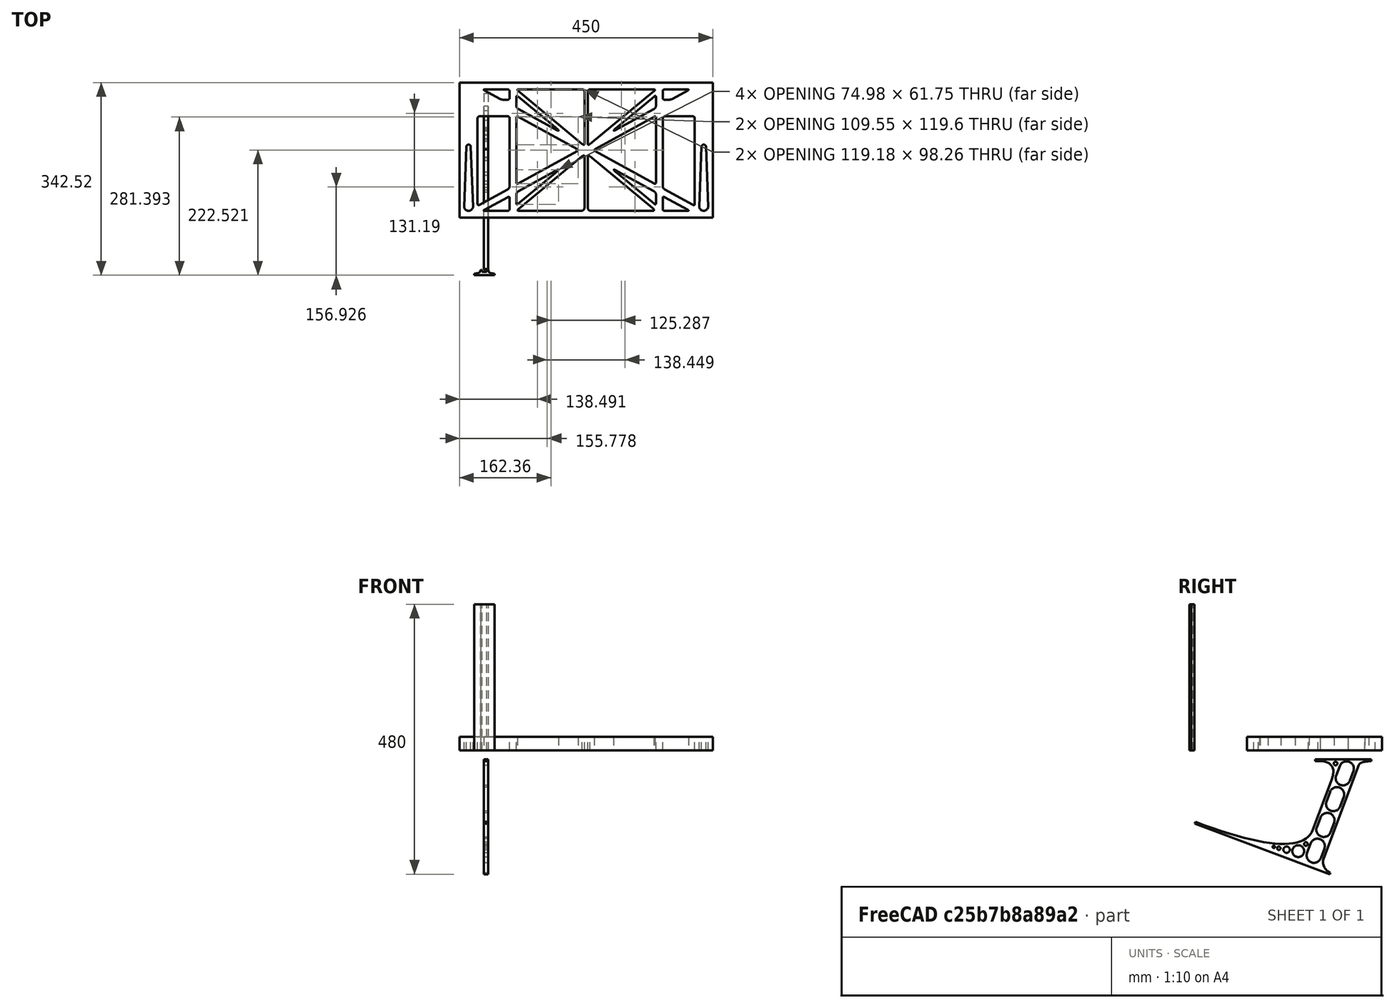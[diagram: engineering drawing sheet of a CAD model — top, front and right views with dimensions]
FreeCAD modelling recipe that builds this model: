
FCSTD DOCUMENT  (FreeCAD 0.19R0.19.2)
Label: laptopStand161FCStd
License: All rights reserved
LicenseURL: http://en.wikipedia.org/wiki/All_rights_reserved
objects: Sketcher::SketchObject×4, Part::Extrusion×3
note: 7 computed .brp shape members not serialized (recipe doc carries the construction recipe); baked Part::Feature solids carry a one-line shape summary decoded from their .brp

FEATURE [Sketcher::SketchObject] Sketch
  FullyConstrained = false
  sketch-geometry (349):
    g0: LineSegment StartX=-10.9272 StartY=-82.7794 StartZ=0 EndX=46.0728 EndY=-51.4823 EndZ=0
    g1: LineSegment StartX=-10.9272 StartY=76.4095 StartZ=0 EndX=-10.9272 EndY=-82.7794 EndZ=0
    g2: LineSegment StartX=46.0728 StartY=76.4095 StartZ=0 EndX=46.0728 EndY=-51.4823 EndZ=0
    g3: LineSegment StartX=-42.9272 StartY=136.221 StartZ=0 EndX=-42.9272 EndY=-103.779 EndZ=0
    g4: LineSegment StartX=407.073 StartY=136.221 StartZ=0 EndX=407.073 EndY=-103.779 EndZ=0
    g5: ArcOfCircle CenterX=-26.9272 CenterY=-83.7794 CenterZ=0 NormalX=0 NormalY=0 NormalZ=1 AngleXU=0 Radius=8 StartAngle=3.14159 EndAngle=6.28319
    g6: ArcOfCircle CenterX=391.073 CenterY=22.1087 CenterZ=0 NormalX=0 NormalY=0 NormalZ=1 AngleXU=0 Radius=8 StartAngle=-4.4e-15 EndAngle=3.14159
    g7: LineSegment StartX=399.073 StartY=22.1087 StartZ=0 EndX=399.073 EndY=-83.7794 EndZ=0
    g8: LineSegment StartX=383.073 StartY=22.1087 StartZ=0 EndX=383.073 EndY=-83.7794 EndZ=0
    g9: ArcOfCircle CenterX=391.073 CenterY=-83.7794 CenterZ=0 NormalX=0 NormalY=0 NormalZ=1 AngleXU=0 Radius=8 StartAngle=3.14159 EndAngle=6.28319
    g10: Circle CenterX=175.022 CenterY=27.0628 CenterZ=0 NormalX=0 NormalY=0 NormalZ=1 AngleXU=0 Radius=1
    g11: Circle CenterX=179.022 CenterY=24.8665 CenterZ=0 NormalX=0 NormalY=0 NormalZ=1 AngleXU=0 Radius=1
    g12: Circle CenterX=179.022 CenterY=27.0628 CenterZ=0 NormalX=0 NormalY=0 NormalZ=1 AngleXU=0 Radius=1
    g13: BSplineCurve PolesCount=3 KnotsCount=2 Degree=2 IsPeriodic=0
    g14: GeomPoint X=175.022 Y=27.0628 Z=0
    g15: GeomPoint X=179.022 Y=27.0628 Z=0
    g16: Circle CenterX=189.124 CenterY=27.0628 CenterZ=0 NormalX=0 NormalY=0 NormalZ=1 AngleXU=0 Radius=1
    g17: Circle CenterX=185.124 CenterY=24.8665 CenterZ=0 NormalX=0 NormalY=0 NormalZ=1 AngleXU=0 Radius=1
    g18: Circle CenterX=185.124 CenterY=27.0628 CenterZ=0 NormalX=0 NormalY=0 NormalZ=1 AngleXU=0 Radius=1
    g19: BSplineCurve PolesCount=3 KnotsCount=2 Degree=2 IsPeriodic=0
    g20: GeomPoint X=189.124 Y=27.0628 Z=0
    g21: GeomPoint X=185.124 Y=27.0628 Z=0
    g22: Circle CenterX=175.022 CenterY=5.37834 CenterZ=0 NormalX=0 NormalY=0 NormalZ=1 AngleXU=0 Radius=1
    g23: Circle CenterX=179.022 CenterY=7.57463 CenterZ=0 NormalX=0 NormalY=0 NormalZ=1 AngleXU=0 Radius=1
    g24: Circle CenterX=179.022 CenterY=5.34704 CenterZ=0 NormalX=0 NormalY=0 NormalZ=1 AngleXU=0 Radius=1
    g25: BSplineCurve PolesCount=3 KnotsCount=2 Degree=2 IsPeriodic=0
    g26: GeomPoint X=175.022 Y=5.37834 Z=0
    g27: GeomPoint X=179.022 Y=5.34704 Z=0
    g28: Circle CenterX=189.124 CenterY=5.37834 CenterZ=0 NormalX=0 NormalY=0 NormalZ=1 AngleXU=0 Radius=1
    g29: Circle CenterX=185.124 CenterY=7.57463 CenterZ=0 NormalX=0 NormalY=0 NormalZ=1 AngleXU=0 Radius=1
    g30: Circle CenterX=185.124 CenterY=5.34704 CenterZ=0 NormalX=0 NormalY=0 NormalZ=1 AngleXU=0 Radius=1
    g31: BSplineCurve PolesCount=3 KnotsCount=2 Degree=2 IsPeriodic=0
    g32: GeomPoint X=189.124 Y=5.37834 Z=0
    g33: GeomPoint X=185.124 Y=5.34704 Z=0
    g34: Circle CenterX=165.871 CenterY=18.1458 CenterZ=0 NormalX=0 NormalY=0 NormalZ=1 AngleXU=0 Radius=1
    g35: Circle CenterX=169.377 CenterY=16.2206 CenterZ=0 NormalX=0 NormalY=0 NormalZ=1 AngleXU=0 Radius=1
    g36: Circle CenterX=165.871 CenterY=14.2954 CenterZ=0 NormalX=0 NormalY=0 NormalZ=1 AngleXU=0 Radius=1
    g37: BSplineCurve PolesCount=3 KnotsCount=2 Degree=2 IsPeriodic=0
    g38: GeomPoint X=165.871 Y=18.1458 Z=0
    g39: GeomPoint X=165.871 Y=14.2954 Z=0
    g40: Circle CenterX=198.275 CenterY=18.1458 CenterZ=0 NormalX=0 NormalY=0 NormalZ=1 AngleXU=0 Radius=1
    g41: Circle CenterX=194.768 CenterY=16.2206 CenterZ=0 NormalX=0 NormalY=0 NormalZ=1 AngleXU=0 Radius=1
    g42: Circle CenterX=198.275 CenterY=14.2954 CenterZ=0 NormalX=0 NormalY=0 NormalZ=1 AngleXU=0 Radius=1
    g43: BSplineCurve PolesCount=3 KnotsCount=2 Degree=2 IsPeriodic=0
    g44: GeomPoint X=198.275 Y=18.1458 Z=0
    g45: GeomPoint X=198.275 Y=14.2954 Z=0
    g46: LineSegment StartX=407.073 StartY=-103.779 StartZ=0 EndX=-42.9272 EndY=-103.779 EndZ=0
    g47: LineSegment StartX=407.073 StartY=136.221 StartZ=0 EndX=-42.9272 EndY=136.221 EndZ=0
    g48: LineSegment StartX=46.0728 StartY=76.4095 StartZ=0 EndX=-10.9272 EndY=76.4095 EndZ=0
    g49: Circle CenterX=125.607 CenterY=54.1951 CenterZ=0 NormalX=0 NormalY=0 NormalZ=1 AngleXU=0 Radius=1
    g50: Circle CenterX=139.632 CenterY=46.4944 CenterZ=0 NormalX=0 NormalY=0 NormalZ=1 AngleXU=0 Radius=1
    g51: Circle CenterX=127.326 CenterY=56.7187 CenterZ=0 NormalX=0 NormalY=0 NormalZ=1 AngleXU=0 Radius=1
    g52: BSplineCurve PolesCount=3 KnotsCount=2 Degree=2 IsPeriodic=0
    g53: GeomPoint X=125.607 Y=54.1951 Z=0
    g54: GeomPoint X=127.326 Y=56.7187 Z=0
    g55: Circle CenterX=236.821 CenterY=56.7187 CenterZ=0 NormalX=0 NormalY=0 NormalZ=1 AngleXU=0 Radius=1
    g56: Circle CenterX=224.513 CenterY=46.4944 CenterZ=0 NormalX=0 NormalY=0 NormalZ=1 AngleXU=0 Radius=1
    g57: Circle CenterX=238.538 CenterY=54.1951 CenterZ=0 NormalX=0 NormalY=0 NormalZ=1 AngleXU=0 Radius=1
    g58: BSplineCurve PolesCount=3 KnotsCount=2 Degree=2 IsPeriodic=0
    g59: GeomPoint X=236.821 Y=56.7187 Z=0
    g60: GeomPoint X=238.538 Y=54.1951 Z=0
    g61: Circle CenterX=238.538 CenterY=-21.7539 CenterZ=0 NormalX=0 NormalY=0 NormalZ=1 AngleXU=0 Radius=1
    g62: Circle CenterX=224.513 CenterY=-14.0532 CenterZ=0 NormalX=0 NormalY=0 NormalZ=1 AngleXU=0 Radius=1
    g63: Circle CenterX=236.821 CenterY=-24.2775 CenterZ=0 NormalX=0 NormalY=0 NormalZ=1 AngleXU=0 Radius=1
    g64: BSplineCurve PolesCount=3 KnotsCount=2 Degree=2 IsPeriodic=0
    g65: GeomPoint X=238.538 Y=-21.7539 Z=0
    g66: GeomPoint X=236.821 Y=-24.2775 Z=0
    g67: Circle CenterX=125.607 CenterY=-21.7539 CenterZ=0 NormalX=0 NormalY=0 NormalZ=1 AngleXU=0 Radius=1
    g68: Circle CenterX=139.632 CenterY=-14.0532 CenterZ=0 NormalX=0 NormalY=0 NormalZ=1 AngleXU=0 Radius=1
    g69: Circle CenterX=127.325 CenterY=-24.2775 CenterZ=0 NormalX=0 NormalY=0 NormalZ=1 AngleXU=0 Radius=1
    g70: BSplineCurve PolesCount=3 KnotsCount=2 Degree=2 IsPeriodic=0
    g71: GeomPoint X=125.607 Y=-21.7539 Z=0
    g72: GeomPoint X=127.325 Y=-24.2775 Z=0
    g73: Circle CenterX=302.996 CenterY=111.695 CenterZ=0 NormalX=0 NormalY=0 NormalZ=1 AngleXU=0 Radius=1
    g74: Circle CenterX=306.073 CenterY=114.251 CenterZ=0 NormalX=0 NormalY=0 NormalZ=1 AngleXU=0 Radius=1
    g75: Circle CenterX=306.073 CenterY=110.251 CenterZ=0 NormalX=0 NormalY=0 NormalZ=1 AngleXU=0 Radius=1
    g76: BSplineCurve PolesCount=3 KnotsCount=2 Degree=2 IsPeriodic=0
    g77: GeomPoint X=302.996 Y=111.695 Z=0
    g78: GeomPoint X=306.073 Y=110.251 Z=0
    g79: Circle CenterX=306.073 CenterY=95.2763 CenterZ=0 NormalX=0 NormalY=0 NormalZ=1 AngleXU=0 Radius=1
    g80: Circle CenterX=306.073 CenterY=91.2763 CenterZ=0 NormalX=0 NormalY=0 NormalZ=1 AngleXU=0 Radius=1
    g81: Circle CenterX=302.567 CenterY=89.3511 CenterZ=0 NormalX=0 NormalY=0 NormalZ=1 AngleXU=0 Radius=1
    g82: BSplineCurve PolesCount=3 KnotsCount=2 Degree=2 IsPeriodic=0
    g83: GeomPoint X=306.073 Y=95.2763 Z=0
    g84: GeomPoint X=302.567 Y=89.3511 Z=0
    g85: LineSegment StartX=306.073 StartY=110.251 StartZ=0 EndX=306.073 EndY=95.2763 EndZ=0
    g86: LineSegment StartX=302.996 StartY=111.695 StartZ=0 EndX=236.821 EndY=56.7187 EndZ=0
    g87: LineSegment StartX=238.538 StartY=54.1951 StartZ=0 EndX=302.567 EndY=89.3511 EndZ=0
    g88: Circle CenterX=61.1496 CenterY=111.695 CenterZ=0 NormalX=0 NormalY=0 NormalZ=1 AngleXU=0 Radius=1
    g89: Circle CenterX=58.0728 CenterY=114.251 CenterZ=0 NormalX=0 NormalY=0 NormalZ=1 AngleXU=0 Radius=1
    g90: Circle CenterX=58.0728 CenterY=110.251 CenterZ=0 NormalX=0 NormalY=0 NormalZ=1 AngleXU=0 Radius=1
    g91: BSplineCurve PolesCount=3 KnotsCount=2 Degree=2 IsPeriodic=0
    g92: GeomPoint X=61.1496 Y=111.695 Z=0
    g93: GeomPoint X=58.0728 Y=110.251 Z=0
    g94: Circle CenterX=61.5791 CenterY=89.3511 CenterZ=0 NormalX=0 NormalY=0 NormalZ=1 AngleXU=0 Radius=1
    g95: Circle CenterX=58.0728 CenterY=91.2763 CenterZ=0 NormalX=0 NormalY=0 NormalZ=1 AngleXU=0 Radius=1
    g96: Circle CenterX=58.0728 CenterY=95.2763 CenterZ=0 NormalX=0 NormalY=0 NormalZ=1 AngleXU=0 Radius=1
    g97: BSplineCurve PolesCount=3 KnotsCount=2 Degree=2 IsPeriodic=0
    g98: GeomPoint X=61.5791 Y=89.3511 Z=0
    g99: GeomPoint X=58.0728 Y=95.2763 Z=0
    g100: LineSegment StartX=58.0728 StartY=110.251 StartZ=0 EndX=58.0728 EndY=95.2763 EndZ=0
    g101: LineSegment StartX=61.1496 StartY=111.695 StartZ=0 EndX=127.326 EndY=56.7187 EndZ=0
    g102: LineSegment StartX=125.607 StartY=54.1951 StartZ=0 EndX=61.5791 EndY=89.3511 EndZ=0
    g103: Circle CenterX=61.5791 CenterY=-56.9099 CenterZ=0 NormalX=0 NormalY=0 NormalZ=1 AngleXU=0 Radius=1
    g104: Circle CenterX=58.0728 CenterY=-58.8351 CenterZ=0 NormalX=0 NormalY=0 NormalZ=1 AngleXU=0 Radius=1
    g105: Circle CenterX=58.0728 CenterY=-62.8351 CenterZ=0 NormalX=0 NormalY=0 NormalZ=1 AngleXU=0 Radius=1
    g106: BSplineCurve PolesCount=3 KnotsCount=2 Degree=2 IsPeriodic=0
    g107: GeomPoint X=61.5791 Y=-56.9099 Z=0
    g108: GeomPoint X=58.0728 Y=-62.8351 Z=0
    g109: Circle CenterX=58.0728 CenterY=-77.8102 CenterZ=0 NormalX=0 NormalY=0 NormalZ=1 AngleXU=0 Radius=1
    g110: Circle CenterX=58.0728 CenterY=-81.8102 CenterZ=0 NormalX=0 NormalY=0 NormalZ=1 AngleXU=0 Radius=1
    g111: Circle CenterX=61.1496 CenterY=-79.2541 CenterZ=0 NormalX=0 NormalY=0 NormalZ=1 AngleXU=0 Radius=1
    g112: BSplineCurve PolesCount=3 KnotsCount=2 Degree=2 IsPeriodic=0
    g113: GeomPoint X=58.0728 Y=-77.8102 Z=0
    g114: GeomPoint X=61.1496 Y=-79.2541 Z=0
    g115: LineSegment StartX=58.0728 StartY=-62.8351 StartZ=0 EndX=58.0728 EndY=-77.8102 EndZ=0
    g116: LineSegment StartX=61.1496 StartY=-79.2541 StartZ=0 EndX=127.325 EndY=-24.2775 EndZ=0
    g117: LineSegment StartX=125.607 StartY=-21.7539 StartZ=0 EndX=61.5791 EndY=-56.9099 EndZ=0
    g118: Circle CenterX=302.567 CenterY=-56.9099 CenterZ=0 NormalX=0 NormalY=0 NormalZ=1 AngleXU=0 Radius=1
    g119: Circle CenterX=306.073 CenterY=-58.8351 CenterZ=0 NormalX=0 NormalY=0 NormalZ=1 AngleXU=0 Radius=1
    g120: Circle CenterX=306.073 CenterY=-62.8351 CenterZ=0 NormalX=0 NormalY=0 NormalZ=1 AngleXU=0 Radius=1
    g121: BSplineCurve PolesCount=3 KnotsCount=2 Degree=2 IsPeriodic=0
    g122: GeomPoint X=302.567 Y=-56.9099 Z=0
    g123: GeomPoint X=306.073 Y=-62.8351 Z=0
    g124: Circle CenterX=302.996 CenterY=-79.2541 CenterZ=0 NormalX=0 NormalY=0 NormalZ=1 AngleXU=0 Radius=1
    g125: Circle CenterX=306.073 CenterY=-81.8102 CenterZ=0 NormalX=0 NormalY=0 NormalZ=1 AngleXU=0 Radius=1
    g126: Circle CenterX=306.073 CenterY=-77.8102 CenterZ=0 NormalX=0 NormalY=0 NormalZ=1 AngleXU=0 Radius=1
    g127: BSplineCurve PolesCount=3 KnotsCount=2 Degree=2 IsPeriodic=0
    g128: GeomPoint X=302.996 Y=-79.2541 Z=0
    g129: GeomPoint X=306.073 Y=-77.8102 Z=0
    g130: LineSegment StartX=306.073 StartY=-62.8351 StartZ=0 EndX=306.073 EndY=-77.8102 EndZ=0
    g131: LineSegment StartX=302.996 StartY=-79.2541 StartZ=0 EndX=236.821 EndY=-24.2775 EndZ=0
    g132: LineSegment StartX=238.538 StartY=-21.7539 StartZ=0 EndX=302.567 EndY=-56.9099 EndZ=0
    g133: Circle CenterX=61.6457 CenterY=-88.8112 CenterZ=0 NormalX=0 NormalY=0 NormalZ=1 AngleXU=0 Radius=1
    g134: Circle CenterX=58.0728 CenterY=-91.7794 CenterZ=0 NormalX=0 NormalY=0 NormalZ=1 AngleXU=0 Radius=1
    g135: Circle CenterX=63.9135 CenterY=-91.7794 CenterZ=0 NormalX=0 NormalY=0 NormalZ=1 AngleXU=0 Radius=1
    g136: BSplineCurve PolesCount=3 KnotsCount=2 Degree=2 IsPeriodic=0
    g137: GeomPoint X=61.6457 Y=-88.8112 Z=0
    g138: GeomPoint X=63.9135 Y=-91.7794 Z=0
    g139: Circle CenterX=179.022 CenterY=-85.8163 CenterZ=0 NormalX=0 NormalY=0 NormalZ=1 AngleXU=0 Radius=1
    g140: Circle CenterX=179.022 CenterY=-91.7794 CenterZ=0 NormalX=0 NormalY=0 NormalZ=1 AngleXU=0 Radius=1
    g141: Circle CenterX=171.895 CenterY=-91.7794 CenterZ=0 NormalX=0 NormalY=0 NormalZ=1 AngleXU=0 Radius=1
    g142: BSplineCurve PolesCount=3 KnotsCount=2 Degree=2 IsPeriodic=0
    g143: GeomPoint X=179.022 Y=-85.8163 Z=0
    g144: GeomPoint X=171.895 Y=-91.7794 Z=0
    g145: Circle CenterX=185.124 CenterY=-86.2028 CenterZ=0 NormalX=0 NormalY=0 NormalZ=1 AngleXU=0 Radius=1
    g146: Circle CenterX=185.124 CenterY=-91.7794 CenterZ=0 NormalX=0 NormalY=0 NormalZ=1 AngleXU=0 Radius=1
    g147: Circle CenterX=191.747 CenterY=-91.7794 CenterZ=0 NormalX=0 NormalY=0 NormalZ=1 AngleXU=0 Radius=1
    g148: BSplineCurve PolesCount=3 KnotsCount=2 Degree=2 IsPeriodic=0
    g149: GeomPoint X=185.124 Y=-86.2028 Z=0
    g150: GeomPoint X=191.747 Y=-91.7794 Z=0
    g151: Circle CenterX=299.888 CenterY=-86.6413 CenterZ=0 NormalX=0 NormalY=0 NormalZ=1 AngleXU=0 Radius=1
    g152: Circle CenterX=306.073 CenterY=-91.7794 CenterZ=0 NormalX=0 NormalY=0 NormalZ=1 AngleXU=0 Radius=1
    g153: Circle CenterX=298.776 CenterY=-91.7794 CenterZ=0 NormalX=0 NormalY=0 NormalZ=1 AngleXU=0 Radius=1
    g154: BSplineCurve PolesCount=3 KnotsCount=2 Degree=2 IsPeriodic=0
    g155: GeomPoint X=299.888 Y=-86.6413 Z=0
    g156: GeomPoint X=298.776 Y=-91.7794 Z=0
    g157: LineSegment StartX=189.124 StartY=5.37834 StartZ=0 EndX=299.888 EndY=-86.6413 EndZ=0
    g158: LineSegment StartX=298.776 StartY=-91.7794 StartZ=0 EndX=191.747 EndY=-91.7794 EndZ=0
    g159: LineSegment StartX=185.124 StartY=-86.2028 StartZ=0 EndX=185.124 EndY=5.34704 EndZ=0
    g160: LineSegment StartX=179.022 StartY=5.34704 StartZ=0 EndX=179.022 EndY=-85.8163 EndZ=0
    g161: LineSegment StartX=171.895 StartY=-91.7794 StartZ=0 EndX=63.9135 EndY=-91.7794 EndZ=0
    g162: LineSegment StartX=61.6457 StartY=-88.8112 StartZ=0 EndX=175.022 EndY=5.37834 EndZ=0
    g163: Circle CenterX=302.073 CenterY=124.221 CenterZ=0 NormalX=0 NormalY=0 NormalZ=1 AngleXU=0 Radius=1
    g164: Circle CenterX=306.073 CenterY=124.221 CenterZ=0 NormalX=0 NormalY=0 NormalZ=1 AngleXU=0 Radius=1
    g165: Circle CenterX=302.996 CenterY=121.665 CenterZ=0 NormalX=0 NormalY=0 NormalZ=1 AngleXU=0 Radius=1
    g166: BSplineCurve PolesCount=3 KnotsCount=2 Degree=2 IsPeriodic=0
    g167: GeomPoint X=302.073 Y=124.221 Z=0
    g168: GeomPoint X=302.996 Y=121.665 Z=0
    g169: Circle CenterX=189.124 CenterY=124.221 CenterZ=0 NormalX=0 NormalY=0 NormalZ=1 AngleXU=0 Radius=1
    g170: Circle CenterX=185.124 CenterY=124.221 CenterZ=0 NormalX=0 NormalY=0 NormalZ=1 AngleXU=0 Radius=1
    g171: Circle CenterX=185.124 CenterY=120.221 CenterZ=0 NormalX=0 NormalY=0 NormalZ=1 AngleXU=0 Radius=1
    g172: BSplineCurve PolesCount=3 KnotsCount=2 Degree=2 IsPeriodic=0
    g173: GeomPoint X=189.124 Y=124.221 Z=0
    g174: GeomPoint X=185.124 Y=120.221 Z=0
    g175: Circle CenterX=175.022 CenterY=124.221 CenterZ=0 NormalX=0 NormalY=0 NormalZ=1 AngleXU=0 Radius=1
    g176: Circle CenterX=179.022 CenterY=124.221 CenterZ=0 NormalX=0 NormalY=0 NormalZ=1 AngleXU=0 Radius=1
    g177: Circle CenterX=179.022 CenterY=120.221 CenterZ=0 NormalX=0 NormalY=0 NormalZ=1 AngleXU=0 Radius=1
    g178: BSplineCurve PolesCount=3 KnotsCount=2 Degree=2 IsPeriodic=0
    g179: GeomPoint X=175.022 Y=124.221 Z=0
    g180: GeomPoint X=179.022 Y=120.221 Z=0
    g181: Circle CenterX=62.0728 CenterY=124.221 CenterZ=0 NormalX=0 NormalY=0 NormalZ=1 AngleXU=0 Radius=1
    g182: Circle CenterX=58.0728 CenterY=124.221 CenterZ=0 NormalX=0 NormalY=0 NormalZ=1 AngleXU=0 Radius=1
    g183: Circle CenterX=61.1496 CenterY=121.665 CenterZ=0 NormalX=0 NormalY=0 NormalZ=1 AngleXU=0 Radius=1
    g184: BSplineCurve PolesCount=3 KnotsCount=2 Degree=2 IsPeriodic=0
    g185: GeomPoint X=62.0728 Y=124.221 Z=0
    g186: GeomPoint X=61.1496 Y=121.665 Z=0
    g187: LineSegment StartX=62.0728 StartY=124.221 StartZ=0 EndX=175.022 EndY=124.221 EndZ=0
    g188: LineSegment StartX=179.022 StartY=120.221 StartZ=0 EndX=179.022 EndY=27.0628 EndZ=0
    g189: LineSegment StartX=185.124 StartY=27.0628 StartZ=0 EndX=185.124 EndY=120.221 EndZ=0
    g190: LineSegment StartX=189.124 StartY=124.221 StartZ=0 EndX=302.073 EndY=124.221 EndZ=0
    g191: LineSegment StartX=302.996 StartY=121.665 StartZ=0 EndX=189.124 EndY=27.0628 EndZ=0
    g192: LineSegment StartX=175.022 StartY=27.0628 StartZ=0 EndX=61.1496 EndY=121.665 EndZ=0
    g193: Circle CenterX=61.5791 CenterY=75.4095 CenterZ=0 NormalX=0 NormalY=0 NormalZ=1 AngleXU=0 Radius=1
    g194: Circle CenterX=58.0728 CenterY=77.3346 CenterZ=0 NormalX=0 NormalY=0 NormalZ=1 AngleXU=0 Radius=1
    g195: Circle CenterX=58.0728 CenterY=73.3346 CenterZ=0 NormalX=0 NormalY=0 NormalZ=1 AngleXU=0 Radius=1
    g196: BSplineCurve PolesCount=3 KnotsCount=2 Degree=2 IsPeriodic=0
    g197: GeomPoint X=61.5791 Y=75.4095 Z=0
    g198: GeomPoint X=58.0728 Y=73.3346 Z=0
    g199: Circle CenterX=58.0728 CenterY=-40.8935 CenterZ=0 NormalX=0 NormalY=0 NormalZ=1 AngleXU=0 Radius=1
    g200: Circle CenterX=58.0728 CenterY=-44.8935 CenterZ=0 NormalX=0 NormalY=0 NormalZ=1 AngleXU=0 Radius=1
    g201: Circle CenterX=61.5791 CenterY=-42.9683 CenterZ=0 NormalX=0 NormalY=0 NormalZ=1 AngleXU=0 Radius=1
    g202: BSplineCurve PolesCount=3 KnotsCount=2 Degree=2 IsPeriodic=0
    g203: GeomPoint X=58.0728 Y=-40.8935 Z=0
    g204: GeomPoint X=61.5791 Y=-42.9683 Z=0
    g205: LineSegment StartX=61.5791 StartY=-42.9683 StartZ=0 EndX=165.871 EndY=14.2954 EndZ=0
    g206: LineSegment StartX=165.871 StartY=18.1458 StartZ=0 EndX=61.5791 EndY=75.4095 EndZ=0
    g207: LineSegment StartX=58.0728 StartY=73.3346 StartZ=0 EndX=58.0728 EndY=-40.8935 EndZ=0
    g208: Circle CenterX=302.567 CenterY=-42.9683 CenterZ=0 NormalX=0 NormalY=0 NormalZ=1 AngleXU=0 Radius=1
    g209: Circle CenterX=306.073 CenterY=-44.8935 CenterZ=0 NormalX=0 NormalY=0 NormalZ=1 AngleXU=0 Radius=1
    g210: Circle CenterX=306.073 CenterY=-40.8935 CenterZ=0 NormalX=0 NormalY=0 NormalZ=1 AngleXU=0 Radius=1
    g211: BSplineCurve PolesCount=3 KnotsCount=2 Degree=2 IsPeriodic=0
    g212: GeomPoint X=302.567 Y=-42.9683 Z=0
    g213: GeomPoint X=306.073 Y=-40.8935 Z=0
    g214: Circle CenterX=306.073 CenterY=73.3346 CenterZ=0 NormalX=0 NormalY=0 NormalZ=1 AngleXU=0 Radius=1
    g215: Circle CenterX=306.073 CenterY=77.3346 CenterZ=0 NormalX=0 NormalY=0 NormalZ=1 AngleXU=0 Radius=1
    g216: Circle CenterX=302.567 CenterY=75.4095 CenterZ=0 NormalX=0 NormalY=0 NormalZ=1 AngleXU=0 Radius=1
    g217: BSplineCurve PolesCount=3 KnotsCount=2 Degree=2 IsPeriodic=0
    g218: GeomPoint X=306.073 Y=73.3346 Z=0
    g219: GeomPoint X=302.567 Y=75.4095 Z=0
    g220: LineSegment StartX=302.567 StartY=-42.9683 StartZ=0 EndX=198.275 EndY=14.2954 EndZ=0
    g221: LineSegment StartX=198.275 StartY=18.1458 StartZ=0 EndX=302.567 EndY=75.4095 EndZ=0
    g222: LineSegment StartX=306.073 StartY=73.3346 StartZ=0 EndX=306.073 EndY=-40.8935 EndZ=0
    g223: LineSegment StartX=322.073 StartY=105.865 StartZ=0 EndX=328.643 EndY=105.865 EndZ=0
    g224: LineSegment StartX=318.073 StartY=120.221 StartZ=0 EndX=318.073 EndY=109.865 EndZ=0
    g225: LineSegment StartX=336.157 StartY=107.779 StartZ=0 EndX=362.567 EndY=122.294 EndZ=0
    g226: Circle CenterX=362.073 CenterY=124.221 CenterZ=0 NormalX=0 NormalY=0 NormalZ=1 AngleXU=0 Radius=1
    g227: Circle CenterX=366.073 CenterY=124.221 CenterZ=0 NormalX=0 NormalY=0 NormalZ=1 AngleXU=0 Radius=1
    g228: Circle CenterX=362.567 CenterY=122.294 CenterZ=0 NormalX=0 NormalY=0 NormalZ=1 AngleXU=0 Radius=1
    g229: BSplineCurve PolesCount=3 KnotsCount=2 Degree=2 IsPeriodic=0
    g230: GeomPoint X=362.073 Y=124.221 Z=0
    g231: GeomPoint X=362.567 Y=122.294 Z=0
    g232: Circle CenterX=322.073 CenterY=124.221 CenterZ=0 NormalX=0 NormalY=0 NormalZ=1 AngleXU=0 Radius=1
    g233: Circle CenterX=318.073 CenterY=124.221 CenterZ=0 NormalX=0 NormalY=0 NormalZ=1 AngleXU=0 Radius=1
    g234: Circle CenterX=318.073 CenterY=120.221 CenterZ=0 NormalX=0 NormalY=0 NormalZ=1 AngleXU=0 Radius=1
    g235: BSplineCurve PolesCount=3 KnotsCount=2 Degree=2 IsPeriodic=0
    g236: GeomPoint X=322.073 Y=124.221 Z=0
    g237: GeomPoint X=318.073 Y=120.221 Z=0
    g238: Circle CenterX=322.073 CenterY=105.865 CenterZ=0 NormalX=0 NormalY=0 NormalZ=1 AngleXU=0 Radius=1
    g239: Circle CenterX=318.073 CenterY=105.865 CenterZ=0 NormalX=0 NormalY=0 NormalZ=1 AngleXU=0 Radius=1
    g240: Circle CenterX=318.073 CenterY=109.865 CenterZ=0 NormalX=0 NormalY=0 NormalZ=1 AngleXU=0 Radius=1
    g241: BSplineCurve PolesCount=3 KnotsCount=2 Degree=2 IsPeriodic=0
    g242: GeomPoint X=322.073 Y=105.865 Z=0
    g243: GeomPoint X=318.073 Y=109.865 Z=0
    g244: Circle CenterX=336.157 CenterY=107.779 CenterZ=0 NormalX=0 NormalY=0 NormalZ=1 AngleXU=0 Radius=1
    g245: Circle CenterX=332.651 CenterY=105.853 CenterZ=0 NormalX=0 NormalY=0 NormalZ=1 AngleXU=0 Radius=1
    g246: Circle CenterX=328.643 CenterY=105.865 CenterZ=0 NormalX=0 NormalY=0 NormalZ=1 AngleXU=0 Radius=1
    g247: BSplineCurve PolesCount=3 KnotsCount=2 Degree=2 IsPeriodic=0
    g248: GeomPoint X=336.157 Y=107.779 Z=0
    g249: GeomPoint X=328.643 Y=105.865 Z=0
    g250: LineSegment StartX=322.073 StartY=124.221 StartZ=0 EndX=362.073 EndY=124.221 EndZ=0
    g251: Circle CenterX=371.567 CenterY=-80.8644 CenterZ=0 NormalX=0 NormalY=0 NormalZ=1 AngleXU=0 Radius=1
    g252: Circle CenterX=375.073 CenterY=-82.7896 CenterZ=0 NormalX=0 NormalY=0 NormalZ=1 AngleXU=0 Radius=1
    g253: Circle CenterX=375.073 CenterY=-78.7896 CenterZ=0 NormalX=0 NormalY=0 NormalZ=1 AngleXU=0 Radius=1
    g254: BSplineCurve PolesCount=3 KnotsCount=2 Degree=2 IsPeriodic=0
    g255: GeomPoint X=371.567 Y=-80.8644 Z=0
    g256: GeomPoint X=375.073 Y=-78.7896 Z=0
    g257: Circle CenterX=321.579 CenterY=-53.4075 CenterZ=0 NormalX=0 NormalY=0 NormalZ=1 AngleXU=0 Radius=1
    g258: Circle CenterX=318.073 CenterY=-51.4823 CenterZ=0 NormalX=0 NormalY=0 NormalZ=1 AngleXU=0 Radius=1
    g259: Circle CenterX=318.073 CenterY=-47.4805 CenterZ=0 NormalX=0 NormalY=0 NormalZ=1 AngleXU=0 Radius=1
    g260: BSplineCurve PolesCount=3 KnotsCount=2 Degree=2 IsPeriodic=0
    g261: GeomPoint X=321.579 Y=-53.4075 Z=0
    g262: GeomPoint X=318.073 Y=-47.4805 Z=0
    g263: LineSegment StartX=371.567 StartY=-80.8644 StartZ=0 EndX=321.579 EndY=-53.4075 EndZ=0
    g264: Circle CenterX=321.579 CenterY=-67.3492 CenterZ=0 NormalX=0 NormalY=0 NormalZ=1 AngleXU=0 Radius=1
    g265: Circle CenterX=318.073 CenterY=-65.424 CenterZ=0 NormalX=0 NormalY=0 NormalZ=1 AngleXU=0 Radius=1
    g266: Circle CenterX=318.073 CenterY=-69.424 CenterZ=0 NormalX=0 NormalY=0 NormalZ=1 AngleXU=0 Radius=1
    g267: BSplineCurve PolesCount=3 KnotsCount=2 Degree=2 IsPeriodic=0
    g268: GeomPoint X=321.579 Y=-67.3492 Z=0
    g269: GeomPoint X=318.073 Y=-69.424 Z=0
    g270: Circle CenterX=362.567 CenterY=-89.8542 CenterZ=0 NormalX=0 NormalY=0 NormalZ=1 AngleXU=0 Radius=1
    g271: Circle CenterX=366.073 CenterY=-91.7794 CenterZ=0 NormalX=0 NormalY=0 NormalZ=1 AngleXU=0 Radius=1
    g272: Circle CenterX=362.073 CenterY=-91.7794 CenterZ=0 NormalX=0 NormalY=0 NormalZ=1 AngleXU=0 Radius=1
    g273: BSplineCurve PolesCount=3 KnotsCount=2 Degree=2 IsPeriodic=0
    g274: GeomPoint X=362.567 Y=-89.8542 Z=0
    g275: GeomPoint X=362.073 Y=-91.7794 Z=0
    g276: Circle CenterX=322.073 CenterY=-91.7794 CenterZ=0 NormalX=0 NormalY=0 NormalZ=1 AngleXU=0 Radius=1
    g277: Circle CenterX=318.073 CenterY=-91.7794 CenterZ=0 NormalX=0 NormalY=0 NormalZ=1 AngleXU=0 Radius=1
    g278: Circle CenterX=318.073 CenterY=-87.7794 CenterZ=0 NormalX=0 NormalY=0 NormalZ=1 AngleXU=0 Radius=1
    g279: BSplineCurve PolesCount=3 KnotsCount=2 Degree=2 IsPeriodic=0
    g280: GeomPoint X=322.073 Y=-91.7794 Z=0
    g281: GeomPoint X=318.073 Y=-87.7794 Z=0
    g282: LineSegment StartX=362.567 StartY=-89.8542 StartZ=0 EndX=321.579 EndY=-67.3492 EndZ=0
    g283: LineSegment StartX=318.073 StartY=-69.424 StartZ=0 EndX=318.073 EndY=-87.7794 EndZ=0
    g284: LineSegment StartX=322.073 StartY=-91.7794 StartZ=0 EndX=362.073 EndY=-91.7794 EndZ=0
    g285: Circle CenterX=2.07281 CenterY=124.221 CenterZ=0 NormalX=0 NormalY=0 NormalZ=1 AngleXU=0 Radius=1
    g286: Circle CenterX=1.57905 CenterY=122.295 CenterZ=0 NormalX=0 NormalY=0 NormalZ=1 AngleXU=0 Radius=1
    g287: BSplineCurve PolesCount=3 KnotsCount=2 Degree=2 IsPeriodic=0
    g288: GeomPoint X=2.07281 Y=124.221 Z=0
    g289: GeomPoint X=1.57905 Y=122.295 Z=0
    g290: Circle CenterX=42.0728 CenterY=124.221 CenterZ=0 NormalX=0 NormalY=0 NormalZ=1 AngleXU=0 Radius=1
    g291: Circle CenterX=46.0728 CenterY=124.221 CenterZ=0 NormalX=0 NormalY=0 NormalZ=1 AngleXU=0 Radius=1
    g292: Circle CenterX=46.0728 CenterY=120.221 CenterZ=0 NormalX=0 NormalY=0 NormalZ=1 AngleXU=0 Radius=1
    g293: BSplineCurve PolesCount=3 KnotsCount=2 Degree=2 IsPeriodic=0
    g294: GeomPoint X=42.0728 Y=124.221 Z=0
    g295: GeomPoint X=46.0728 Y=120.221 Z=0
    g296: Circle CenterX=46.0728 CenterY=109.865 CenterZ=0 NormalX=0 NormalY=0 NormalZ=1 AngleXU=0 Radius=1
    g297: Circle CenterX=46.0728 CenterY=105.865 CenterZ=0 NormalX=0 NormalY=0 NormalZ=1 AngleXU=0 Radius=1
    g298: Circle CenterX=42.0728 CenterY=105.865 CenterZ=0 NormalX=0 NormalY=0 NormalZ=1 AngleXU=0 Radius=1
    g299: BSplineCurve PolesCount=3 KnotsCount=2 Degree=2 IsPeriodic=0
    g300: GeomPoint X=46.0728 Y=109.865 Z=0
    g301: GeomPoint X=42.0728 Y=105.865 Z=0
    g302: Circle CenterX=35.5028 CenterY=105.865 CenterZ=0 NormalX=0 NormalY=0 NormalZ=1 AngleXU=0 Radius=1
    g303: Circle CenterX=31.5028 CenterY=105.865 CenterZ=0 NormalX=0 NormalY=0 NormalZ=1 AngleXU=0 Radius=1
    g304: Circle CenterX=27.9965 CenterY=107.79 CenterZ=0 NormalX=0 NormalY=0 NormalZ=1 AngleXU=0 Radius=1
    g305: BSplineCurve PolesCount=3 KnotsCount=2 Degree=2 IsPeriodic=0
    g306: GeomPoint X=35.5028 Y=105.865 Z=0
    g307: GeomPoint X=27.9965 Y=107.79 Z=0
    g308: LineSegment StartX=2.07281 StartY=124.221 StartZ=0 EndX=42.0728 EndY=124.221 EndZ=0
    g309: LineSegment StartX=46.0728 StartY=120.221 StartZ=0 EndX=46.0728 EndY=109.865 EndZ=0
    g310: LineSegment StartX=42.0728 StartY=105.865 StartZ=0 EndX=35.5028 EndY=105.865 EndZ=0
    g311: LineSegment StartX=27.9965 StartY=107.79 StartZ=0 EndX=1.57905 EndY=122.295 EndZ=0
    g312: Circle CenterX=42.5666 CenterY=-67.3492 CenterZ=0 NormalX=0 NormalY=0 NormalZ=1 AngleXU=0 Radius=1
    g313: Circle CenterX=46.0728 CenterY=-65.424 CenterZ=0 NormalX=0 NormalY=0 NormalZ=1 AngleXU=0 Radius=1
    g314: Circle CenterX=46.0728 CenterY=-69.424 CenterZ=0 NormalX=0 NormalY=0 NormalZ=1 AngleXU=0 Radius=1
    g315: BSplineCurve PolesCount=3 KnotsCount=2 Degree=2 IsPeriodic=0
    g316: GeomPoint X=42.5666 Y=-67.3492 Z=0
    g317: GeomPoint X=46.0728 Y=-69.424 Z=0
    g318: Circle CenterX=46.0728 CenterY=-87.7794 CenterZ=0 NormalX=0 NormalY=0 NormalZ=1 AngleXU=0 Radius=1
    g319: Circle CenterX=46.0728 CenterY=-91.7794 CenterZ=0 NormalX=0 NormalY=0 NormalZ=1 AngleXU=0 Radius=1
    g320: Circle CenterX=42.0728 CenterY=-91.7794 CenterZ=0 NormalX=0 NormalY=0 NormalZ=1 AngleXU=0 Radius=1
    g321: BSplineCurve PolesCount=3 KnotsCount=2 Degree=2 IsPeriodic=0
    g322: GeomPoint X=46.0728 Y=-87.7794 Z=0
    g323: GeomPoint X=42.0728 Y=-91.7794 Z=0
    g324: Circle CenterX=2.07281 CenterY=-91.7794 CenterZ=0 NormalX=0 NormalY=0 NormalZ=1 AngleXU=0 Radius=1
    g325: Circle CenterX=-1.92719 CenterY=-91.7794 CenterZ=0 NormalX=0 NormalY=0 NormalZ=1 AngleXU=0 Radius=1
    g326: Circle CenterX=1.57905 CenterY=-89.8542 CenterZ=0 NormalX=0 NormalY=0 NormalZ=1 AngleXU=0 Radius=1
    g327: BSplineCurve PolesCount=3 KnotsCount=2 Degree=2 IsPeriodic=0
    g328: GeomPoint X=2.07281 Y=-91.7794 Z=0
    g329: GeomPoint X=1.57905 Y=-89.8542 Z=0
    g330: LineSegment StartX=2.07281 StartY=-91.7794 StartZ=0 EndX=42.0728 EndY=-91.7794 EndZ=0
    g331: LineSegment StartX=46.0728 StartY=-87.7794 StartZ=0 EndX=46.0728 EndY=-69.424 EndZ=0
    g332: LineSegment StartX=42.5666 StartY=-67.3492 StartZ=0 EndX=1.57905 EndY=-89.8542 EndZ=0
    g333: Circle CenterX=322.073 CenterY=76.4095 CenterZ=0 NormalX=0 NormalY=0 NormalZ=1 AngleXU=0 Radius=4
    g334: BSplineCurve PolesCount=3 KnotsCount=2 Degree=2 IsPeriodic=0
    g335: GeomPoint X=318.073 Y=72.4095 Z=0
    g336: GeomPoint X=322.073 Y=76.4095 Z=0
    g337: Circle CenterX=375.073 CenterY=72.4095 CenterZ=0 NormalX=0 NormalY=0 NormalZ=1 AngleXU=0 Radius=1
    g338: Circle CenterX=375.073 CenterY=76.4095 CenterZ=0 NormalX=0 NormalY=0 NormalZ=1 AngleXU=0 Radius=1
    g339: Circle CenterX=371.073 CenterY=76.4095 CenterZ=0 NormalX=0 NormalY=0 NormalZ=1 AngleXU=0 Radius=1
    g340: BSplineCurve PolesCount=3 KnotsCount=2 Degree=2 IsPeriodic=0
    g341: GeomPoint X=375.073 Y=72.4095 Z=0
    g342: GeomPoint X=371.073 Y=76.4095 Z=0
    g343: LineSegment StartX=322.073 StartY=76.4095 StartZ=0 EndX=371.073 EndY=76.4095 EndZ=0
    g344: LineSegment StartX=318.073 StartY=72.4095 StartZ=0 EndX=318.073 EndY=-47.4805 EndZ=0
    g345: LineSegment StartX=375.073 StartY=72.4095 StartZ=0 EndX=375.073 EndY=-78.7896 EndZ=0
    g346: ArcOfCircle CenterX=-26.9272 CenterY=22.1087 CenterZ=0 NormalX=0 NormalY=0 NormalZ=1 AngleXU=0 Radius=4 StartAngle=5e-16 EndAngle=3.14159
    g347: LineSegment StartX=-30.9272 StartY=22.1087 StartZ=0 EndX=-34.9272 EndY=-83.7794 EndZ=0
    g348: LineSegment StartX=-18.9272 StartY=-83.7794 StartZ=0 EndX=-22.9272 EndY=22.1087 EndZ=0
  constraints (572):
    c: Coincident(g0,g2)
    c: Block(g0)
    c: Block(g1)
    c: Vertical(g3)
    c: Vertical(g4)
    c: Block(g4)
    c: Block(g3)
    c: Tangent(g6,g7) = 1.5708
    c: Tangent(g7,g9) = 1.5708
    c: Equal(g6,g9)
    c: Coincident(g8,g6)
    c: Coincident(g8,g9)
    c: Block(g7)
    c: Block(g8)
    c: Weight(g10) = 1
    c: Equal(g10,g11)
    c: Equal(g10,g12)
    c: InternalAlignment(g10,g13)
    c: InternalAlignment(g11,g13)
    c: InternalAlignment(g12,g13)
    c: InternalAlignment(g14,g13)
    c: InternalAlignment(g15,g13)
    c: Weight(g16) = 1
    c: Equal(g16,g17)
    c: Equal(g16,g18)
    c: InternalAlignment(g16,g19)
    c: InternalAlignment(g17,g19)
    c: InternalAlignment(g18,g19)
    c: InternalAlignment(g20,g19)
    c: InternalAlignment(g21,g19)
    c: Block(g19)
    c: Block(g13)
    c: Weight(g22) = 1
    c: Equal(g22,g23)
    c: Equal(g22,g24)
    c: InternalAlignment(g22,g25)
    c: InternalAlignment(g23,g25)
    c: InternalAlignment(g24,g25)
    c: InternalAlignment(g26,g25)
    c: InternalAlignment(g27,g25)
    c: Weight(g28) = 1
    c: Equal(g28,g29)
    c: Equal(g28,g30)
    c: InternalAlignment(g28,g31)
    c: InternalAlignment(g29,g31)
    c: InternalAlignment(g30,g31)
    c: InternalAlignment(g32,g31)
    c: InternalAlignment(g33,g31)
    c: Block(g31)
    c: Block(g25)
    c: Weight(g34) = 1
    c: Equal(g34,g35)
    c: Equal(g34,g36)
    c: InternalAlignment(g34,g37)
    c: InternalAlignment(g35,g37)
    c: InternalAlignment(g36,g37)
    c: InternalAlignment(g38,g37)
    c: InternalAlignment(g39,g37)
    c: Weight(g40) = 1
    c: Equal(g40,g41)
    c: Equal(g40,g42)
    c: InternalAlignment(g40,g43)
    c: InternalAlignment(g41,g43)
    c: InternalAlignment(g42,g43)
    c: InternalAlignment(g44,g43)
    c: InternalAlignment(g45,g43)
    c: Block(g37)
    c: Block(g43)
    c: Coincident(g46,g4)
    c: Coincident(g46,g3)
    c: Horizontal(g46)
    c: Distance(g46) = 450
    c: Coincident(g47,g4)
    c: Coincident(g47,g3)
    c: Horizontal(g47)
    c: Horizontal(g48)
    c: Coincident(g2,g48)
    c: Block(g48)
    c: Coincident(g1,g48)
    c: Weight(g49) = 1
    c: Equal(g49,g50)
    c: Equal(g49,g51)
    c: InternalAlignment(g49,g52)
    c: InternalAlignment(g50,g52)
    c: InternalAlignment(g51,g52)
    c: InternalAlignment(g53,g52)
    c: InternalAlignment(g54,g52)
    c: Block(g52)
    c: Weight(g55) = 1
    c: Equal(g55,g56)
    c: Equal(g55,g57)
    c: InternalAlignment(g55,g58)
    c: InternalAlignment(g56,g58)
    c: InternalAlignment(g57,g58)
    c: InternalAlignment(g59,g58)
    c: InternalAlignment(g60,g58)
    c: Block(g58)
    c: Weight(g61) = 1
    c: Equal(g61,g62)
    c: Equal(g61,g63)
    c: InternalAlignment(g61,g64)
    c: InternalAlignment(g62,g64)
    c: InternalAlignment(g63,g64)
    c: InternalAlignment(g65,g64)
    c: InternalAlignment(g66,g64)
    c: Block(g64)
    c: Weight(g67) = 1
    c: Equal(g67,g68)
    c: Equal(g67,g69)
    c: InternalAlignment(g67,g70)
    c: InternalAlignment(g68,g70)
    c: InternalAlignment(g69,g70)
    c: InternalAlignment(g71,g70)
    c: InternalAlignment(g72,g70)
    c: Block(g70)
    c: Weight(g73) = 1
    c: Equal(g73,g74)
    c: Equal(g73,g75)
    c: InternalAlignment(g73,g76)
    c: InternalAlignment(g74,g76)
    c: InternalAlignment(g75,g76)
    c: InternalAlignment(g77,g76)
    c: InternalAlignment(g78,g76)
    c: Weight(g79) = 1
    c: Equal(g79,g80)
    c: Equal(g79,g81)
    c: InternalAlignment(g79,g82)
    c: InternalAlignment(g80,g82)
    c: InternalAlignment(g81,g82)
    c: InternalAlignment(g83,g82)
    c: InternalAlignment(g84,g82)
    c: Block(g76)
    c: Block(g82)
    c: Coincident(g85,g76)
    c: Coincident(g85,g82)
    c: Vertical(g85)
    c: Coincident(g86,g76)
    c: Coincident(g86,g58)
    c: Coincident(g87,g58)
    c: Coincident(g87,g82)
    c: Weight(g88) = 1
    c: Equal(g88,g89)
    c: Equal(g88,g90)
    c: InternalAlignment(g88,g91)
    c: InternalAlignment(g89,g91)
    c: InternalAlignment(g90,g91)
    c: InternalAlignment(g92,g91)
    c: InternalAlignment(g93,g91)
    c: Weight(g94) = 1
    c: Equal(g94,g95)
    c: Equal(g94,g96)
    c: InternalAlignment(g94,g97)
    c: InternalAlignment(g95,g97)
    c: InternalAlignment(g96,g97)
    c: InternalAlignment(g98,g97)
    c: InternalAlignment(g99,g97)
    c: Block(g91)
    c: Block(g97)
    c: Coincident(g100,g91)
    c: Coincident(g100,g97)
    c: Vertical(g100)
    c: Coincident(g101,g91)
    c: Coincident(g101,g52)
    c: Coincident(g102,g52)
    c: Coincident(g102,g97)
    c: Weight(g103) = 1
    c: Equal(g103,g104)
    c: Equal(g103,g105)
    c: InternalAlignment(g103,g106)
    c: InternalAlignment(g104,g106)
    c: InternalAlignment(g105,g106)
    c: InternalAlignment(g107,g106)
    c: InternalAlignment(g108,g106)
    c: Weight(g109) = 1
    c: Equal(g109,g110)
    c: Equal(g109,g111)
    c: InternalAlignment(g109,g112)
    c: InternalAlignment(g110,g112)
    c: InternalAlignment(g111,g112)
    c: InternalAlignment(g113,g112)
    c: InternalAlignment(g114,g112)
    c: Block(g106)
    c: Block(g112)
    c: Coincident(g115,g106)
    c: Coincident(g115,g112)
    c: Vertical(g115)
    c: Coincident(g116,g112)
    c: Coincident(g116,g70)
    c: Coincident(g117,g70)
    c: Coincident(g117,g106)
    c: Weight(g118) = 1
    c: Equal(g118,g119)
    c: Equal(g118,g120)
    c: InternalAlignment(g118,g121)
    c: InternalAlignment(g119,g121)
    c: InternalAlignment(g120,g121)
    c: InternalAlignment(g122,g121)
    c: InternalAlignment(g123,g121)
    c: Weight(g124) = 1
    c: Equal(g124,g125)
    c: Equal(g124,g126)
    c: InternalAlignment(g124,g127)
    c: InternalAlignment(g125,g127)
    c: InternalAlignment(g126,g127)
    c: InternalAlignment(g128,g127)
    c: InternalAlignment(g129,g127)
    c: Block(g121)
    c: Block(g127)
    c: Coincident(g130,g121)
    c: Coincident(g130,g127)
    c: Vertical(g130)
    c: Coincident(g131,g127)
    c: Coincident(g131,g64)
    c: Coincident(g132,g64)
    c: Coincident(g132,g121)
    c: Weight(g133) = 1
    c: Equal(g133,g134)
    c: Equal(g133,g135)
    c: InternalAlignment(g133,g136)
    c: InternalAlignment(g134,g136)
    c: InternalAlignment(g135,g136)
    c: InternalAlignment(g137,g136)
    c: InternalAlignment(g138,g136)
    c: Weight(g139) = 1
    c: Equal(g139,g140)
    c: Equal(g139,g141)
    c: InternalAlignment(g139,g142)
    c: InternalAlignment(g140,g142)
    c: InternalAlignment(g141,g142)
    c: InternalAlignment(g143,g142)
    c: InternalAlignment(g144,g142)
    c: Weight(g145) = 1
    c: Equal(g145,g146)
    c: Equal(g145,g147)
    c: InternalAlignment(g145,g148)
    c: InternalAlignment(g146,g148)
    c: InternalAlignment(g147,g148)
    c: InternalAlignment(g149,g148)
    c: InternalAlignment(g150,g148)
    c: Weight(g151) = 1
    c: Equal(g151,g152)
    c: Equal(g151,g153)
    c: InternalAlignment(g151,g154)
    c: InternalAlignment(g152,g154)
    c: InternalAlignment(g153,g154)
    c: InternalAlignment(g155,g154)
    c: InternalAlignment(g156,g154)
    c: Block(g154)
    c: Block(g148)
    c: Block(g142)
    c: Block(g136)
    c: Coincident(g157,g31)
    c: Coincident(g157,g154)
    c: Coincident(g158,g154)
    c: Coincident(g158,g148)
    c: Horizontal(g158)
    c: Coincident(g159,g148)
    c: Coincident(g159,g31)
    c: Vertical(g159)
    c: Coincident(g160,g25)
    c: Coincident(g160,g142)
    c: Vertical(g160)
    c: Coincident(g161,g142)
    c: Coincident(g161,g136)
    c: Horizontal(g161)
    c: Coincident(g162,g136)
    c: Coincident(g162,g25)
    c: Weight(g163) = 1
    c: Equal(g163,g164)
    c: Equal(g163,g165)
    c: InternalAlignment(g163,g166)
    c: InternalAlignment(g164,g166)
    c: InternalAlignment(g165,g166)
    c: InternalAlignment(g167,g166)
    c: InternalAlignment(g168,g166)
    c: Weight(g169) = 1
    c: Equal(g169,g170)
    c: Equal(g169,g171)
    c: InternalAlignment(g169,g172)
    c: InternalAlignment(g170,g172)
    c: InternalAlignment(g171,g172)
    c: InternalAlignment(g173,g172)
    c: InternalAlignment(g174,g172)
    c: Weight(g175) = 1
    c: Equal(g175,g176)
    c: Equal(g175,g177)
    c: InternalAlignment(g175,g178)
    c: InternalAlignment(g176,g178)
    c: InternalAlignment(g177,g178)
    c: InternalAlignment(g179,g178)
    c: InternalAlignment(g180,g178)
    c: Weight(g181) = 1
    c: Equal(g181,g182)
    c: Equal(g181,g183)
    c: InternalAlignment(g181,g184)
    c: InternalAlignment(g182,g184)
    c: InternalAlignment(g183,g184)
    c: InternalAlignment(g185,g184)
    c: InternalAlignment(g186,g184)
    c: Block(g184)
    c: Block(g178)
    c: Block(g172)
    c: Block(g166)
    c: Coincident(g187,g184)
    c: Coincident(g187,g178)
    c: Horizontal(g187)
    c: Coincident(g188,g178)
    c: Coincident(g188,g13)
    c: Vertical(g188)
    c: Coincident(g189,g19)
    c: Coincident(g189,g172)
    c: Vertical(g189)
    c: Coincident(g190,g172)
    c: Coincident(g190,g166)
    c: Horizontal(g190)
    c: Coincident(g191,g166)
    c: Coincident(g191,g19)
    c: Coincident(g192,g13)
    c: Weight(g193) = 1
    c: Equal(g193,g194)
    c: Equal(g193,g195)
    c: InternalAlignment(g193,g196)
    c: InternalAlignment(g194,g196)
    c: InternalAlignment(g195,g196)
    c: InternalAlignment(g197,g196)
    c: InternalAlignment(g198,g196)
    c: Weight(g199) = 1
    c: Equal(g199,g200)
    c: Equal(g199,g201)
    c: InternalAlignment(g199,g202)
    c: InternalAlignment(g200,g202)
    c: InternalAlignment(g201,g202)
    c: InternalAlignment(g203,g202)
    c: InternalAlignment(g204,g202)
    c: Block(g202)
    c: Block(g196)
    c: Coincident(g205,g202)
    c: Coincident(g205,g37)
    c: Coincident(g206,g37)
    c: Coincident(g206,g196)
    c: Coincident(g207,g196)
    c: Coincident(g207,g202)
    c: Vertical(g207)
    c: Weight(g208) = 1
    c: Equal(g208,g209)
    c: Equal(g208,g210)
    c: InternalAlignment(g208,g211)
    c: InternalAlignment(g209,g211)
    c: InternalAlignment(g210,g211)
    c: InternalAlignment(g212,g211)
    c: InternalAlignment(g213,g211)
    c: Weight(g214) = 1
    c: Equal(g214,g215)
    c: Equal(g214,g216)
    c: InternalAlignment(g214,g217)
    c: InternalAlignment(g215,g217)
    c: InternalAlignment(g216,g217)
    c: InternalAlignment(g218,g217)
    c: InternalAlignment(g219,g217)
    c: Block(g217)
    c: Block(g211)
    c: Coincident(g220,g211)
    c: Coincident(g220,g43)
    c: Coincident(g221,g43)
    c: Coincident(g221,g217)
    c: Coincident(g222,g217)
    c: Coincident(g222,g211)
    c: Vertical(g222)
    c: Horizontal(g223)
    c: Block(g223)
    c: Vertical(g224)
    c: Block(g224)
    c: Block(g225)
    c: Weight(g226) = 1
    c: Equal(g226,g227)
    c: Equal(g226,g228)
    c: InternalAlignment(g226,g229)
    c: InternalAlignment(g227,g229)
    c: InternalAlignment(g228,g229)
    c: InternalAlignment(g230,g229)
    c: InternalAlignment(g231,g229)
    c: Weight(g232) = 1
    c: Equal(g232,g233)
    c: Equal(g232,g234)
    c: InternalAlignment(g232,g235)
    c: InternalAlignment(g233,g235)
    c: InternalAlignment(g234,g235)
    c: InternalAlignment(g236,g235)
    c: InternalAlignment(g237,g235)
    c: Weight(g238) = 1
    c: Equal(g238,g239)
    c: Equal(g238,g240)
    c: InternalAlignment(g238,g241)
    c: InternalAlignment(g239,g241)
    c: InternalAlignment(g240,g241)
    c: InternalAlignment(g242,g241)
    c: InternalAlignment(g243,g241)
    c: Weight(g244) = 1
    c: Equal(g244,g245)
    c: Equal(g244,g246)
    c: InternalAlignment(g244,g247)
    c: InternalAlignment(g245,g247)
    c: InternalAlignment(g246,g247)
    c: InternalAlignment(g248,g247)
    c: InternalAlignment(g249,g247)
    c: Block(g229)
    c: Block(g235)
    c: Block(g241)
    c: Block(g247)
    c: Coincident(g250,g235)
    c: Coincident(g250,g229)
    c: Horizontal(g250)
    c: Block(g192)
    c: Weight(g251) = 1
    c: Equal(g251,g252)
    c: Equal(g251,g253)
    c: InternalAlignment(g251,g254)
    c: InternalAlignment(g252,g254)
    c: InternalAlignment(g253,g254)
    c: InternalAlignment(g255,g254)
    c: InternalAlignment(g256,g254)
    c: Weight(g257) = 1
    c: Equal(g257,g258)
    c: Equal(g257,g259)
    c: InternalAlignment(g257,g260)
    c: InternalAlignment(g258,g260)
    c: InternalAlignment(g259,g260)
    c: InternalAlignment(g261,g260)
    c: InternalAlignment(g262,g260)
    c: Block(g254)
    c: Block(g260)
    c: Coincident(g263,g254)
    c: Coincident(g263,g260)
    c: Weight(g264) = 1
    c: Equal(g264,g265)
    c: Equal(g264,g266)
    c: InternalAlignment(g264,g267)
    c: InternalAlignment(g265,g267)
    c: InternalAlignment(g266,g267)
    c: InternalAlignment(g268,g267)
    c: InternalAlignment(g269,g267)
    c: Weight(g270) = 1
    c: Equal(g270,g271)
    c: Equal(g270,g272)
    c: InternalAlignment(g270,g273)
    c: InternalAlignment(g271,g273)
    c: InternalAlignment(g272,g273)
    c: InternalAlignment(g274,g273)
    c: InternalAlignment(g275,g273)
    c: Weight(g276) = 1
    c: Equal(g276,g277)
    c: Equal(g276,g278)
    c: InternalAlignment(g276,g279)
    c: InternalAlignment(g277,g279)
    c: InternalAlignment(g278,g279)
    c: InternalAlignment(g280,g279)
    c: InternalAlignment(g281,g279)
    c: Block(g279)
    c: Block(g273)
    c: Block(g267)
    c: Coincident(g282,g273)
    c: Coincident(g282,g267)
    c: Coincident(g283,g267)
    c: Coincident(g283,g279)
    c: Vertical(g283)
    c: Coincident(g284,g279)
    c: Coincident(g284,g273)
    c: Horizontal(g284)
    c: Weight(g285) = 1
    c: Equal(g285,g286)
    c: InternalAlignment(g285,g287)
    c: InternalAlignment(g286,g287)
    c: InternalAlignment(g288,g287)
    c: InternalAlignment(g289,g287)
    c: Weight(g290) = 1
    c: InternalAlignment(g291,g293)
    c: InternalAlignment(g292,g293)
    c: InternalAlignment(g294,g293)
    c: InternalAlignment(g295,g293)
    c: Weight(g296) = 1
    c: Equal(g296,g297)
    c: Equal(g296,g298)
    c: InternalAlignment(g296,g299)
    c: InternalAlignment(g297,g299)
    c: InternalAlignment(g298,g299)
    c: InternalAlignment(g300,g299)
    c: InternalAlignment(g301,g299)
    c: Equal(g302,g303)
    c: Equal(g302,g304)
    c: InternalAlignment(g302,g305)
    c: InternalAlignment(g303,g305)
    c: InternalAlignment(g304,g305)
    c: InternalAlignment(g306,g305)
    c: InternalAlignment(g307,g305)
    c: Block(g293)
    c: Block(g299)
    c: Block(g305)
    c: Block(g287)
    c: Coincident(g308,g287)
    c: Coincident(g308,g293)
    c: Horizontal(g308)
    c: Coincident(g309,g293)
    c: Coincident(g309,g299)
    c: Vertical(g309)
    c: Coincident(g310,g299)
    c: Coincident(g310,g305)
    c: Horizontal(g310)
    c: Coincident(g311,g305)
    c: Coincident(g311,g287)
    c: Weight(g312) = 1
    c: Equal(g312,g313)
    c: Equal(g312,g314)
    c: InternalAlignment(g312,g315)
    c: InternalAlignment(g313,g315)
    c: InternalAlignment(g314,g315)
    c: InternalAlignment(g316,g315)
    c: InternalAlignment(g317,g315)
    c: Weight(g318) = 1
    c: Equal(g318,g319)
    c: Equal(g318,g320)
    c: InternalAlignment(g318,g321)
    c: InternalAlignment(g319,g321)
    c: InternalAlignment(g320,g321)
    c: InternalAlignment(g322,g321)
    c: InternalAlignment(g323,g321)
    c: Weight(g324) = 1
    c: Equal(g324,g325)
    c: Equal(g324,g326)
    c: InternalAlignment(g324,g327)
    c: InternalAlignment(g325,g327)
    c: InternalAlignment(g326,g327)
    c: InternalAlignment(g328,g327)
    c: InternalAlignment(g329,g327)
    c: Block(g327)
    c: Block(g321)
    c: Block(g315)
    c: Coincident(g330,g327)
    c: Coincident(g330,g321)
    c: Horizontal(g330)
    c: Coincident(g331,g321)
    c: Coincident(g331,g315)
    c: Vertical(g331)
    c: Coincident(g332,g315)
    c: Coincident(g332,g327)
    c: InternalAlignment(g333,g334)
    c: InternalAlignment(g335,g334)
    c: InternalAlignment(g336,g334)
    c: Block(g334)
    c: Equal(g337,g338)
    c: Equal(g337,g339)
    c: InternalAlignment(g337,g340)
    c: InternalAlignment(g338,g340)
    c: InternalAlignment(g339,g340)
    c: InternalAlignment(g341,g340)
    c: InternalAlignment(g342,g340)
    c: Block(g340)
    c: Coincident(g343,g334)
    c: Horizontal(g343)
    c: Block(g343)
    c: Coincident(g344,g334)
    c: Coincident(g344,g260)
    c: Vertical(g344)
    c: Coincident(g345,g340)
    c: Coincident(g345,g254)
    c: Vertical(g345)
    c: Coincident(g347,g5)
    c: Coincident(g348,g5)
    c: Block(g346)
    c: Block(g5)
    c: Block(g348)
    c: Block(g347)
    c: Distance(g344) = 119.89
FEATURE [Sketcher::SketchObject] Sketch001
  FullyConstrained = true
  MapMode = 4
  Placement = pos=(0,0,0) rot=(0.57735,0.57735,0.57735;2.0944rad)
  Support = -> [Sketch]
  sketch-geometry (46):
    g0: BSplineCurve PolesCount=3 KnotsCount=2 Degree=2 IsPeriodic=0
    g1: ArcOfCircle CenterX=73.1223 CenterY=-32.291 CenterZ=0 NormalX=0 NormalY=0 NormalZ=1 AngleXU=0 Radius=13 StartAngle=5.92268 EndAngle=9.06428
    g2: ArcOfCircle CenterX=66.7816 CenterY=-49.1439 CenterZ=0 NormalX=0 NormalY=0 NormalZ=1 AngleXU=0 Radius=13 StartAngle=2.78068 EndAngle=5.92131
    g3: ArcOfCircle CenterX=55.9263 CenterY=-78.1807 CenterZ=0 NormalX=0 NormalY=0 NormalZ=1 AngleXU=0 Radius=13 StartAngle=5.92268 EndAngle=9.06428
    g4: ArcOfCircle CenterX=49.5884 CenterY=-95.0342 CenterZ=0 NormalX=0 NormalY=0 NormalZ=1 AngleXU=0 Radius=13 StartAngle=2.78068 EndAngle=5.92131
    g5: ArcOfCircle CenterX=38.7206 CenterY=-124.067 CenterZ=0 NormalX=0 NormalY=0 NormalZ=1 AngleXU=0 Radius=13 StartAngle=5.92268 EndAngle=9.06428
    g6: ArcOfCircle CenterX=32.3875 CenterY=-140.92 CenterZ=0 NormalX=0 NormalY=0 NormalZ=1 AngleXU=0 Radius=13 StartAngle=2.78068 EndAngle=5.92131
    g7: ArcOfCircle CenterX=21.4715 CenterY=-169.934 CenterZ=0 NormalX=0 NormalY=0 NormalZ=1 AngleXU=0 Radius=13 StartAngle=5.92268 EndAngle=9.06428
    g8: ArcOfCircle CenterX=15.1336 CenterY=-186.787 CenterZ=0 NormalX=0 NormalY=0 NormalZ=1 AngleXU=0 Radius=13 StartAngle=2.78068 EndAngle=5.92131
    g9-g12: Circle x4 (B-spline internal-alignment scaffolding for g13; pole/knot coordinates omitted)
    g13: BSplineCurve PolesCount=4 KnotsCount=2 Degree=3 IsPeriodic=0
    g14: GeomPoint X=28.8094 Y=-19.0875 Z=0
    g15: GeomPoint X=47.0443 Y=-50.4712 Z=0
    g16: Circle CenterX=53.5586 CenterY=-23.2695 CenterZ=0 NormalX=0 NormalY=0 NormalZ=1 AngleXU=0 Radius=3.24518
    g17: Circle CenterX=-195.441 CenterY=-127.082 CenterZ=0 NormalX=0 NormalY=0 NormalZ=1 AngleXU=0 Radius=1
    g18: Circle CenterX=-8.24091 CenterY=-197.481 CenterZ=0 NormalX=0 NormalY=0 NormalZ=1 AngleXU=0 Radius=1
    g19: Circle CenterX=12.8789 CenterY=-141.321 CenterZ=0 NormalX=0 NormalY=0 NormalZ=1 AngleXU=0 Radius=1
    g20: BSplineCurve PolesCount=3 KnotsCount=2 Degree=2 IsPeriodic=0
    g21: GeomPoint X=-195.441 Y=-127.082 Z=0
    g22: GeomPoint X=12.8789 Y=-141.321 Z=0
    g23: Circle CenterX=-12.8016 CenterY=-179.036 CenterZ=0 NormalX=0 NormalY=0 NormalZ=1 AngleXU=0 Radius=10.5072
    g24: Circle CenterX=0.933922 CenterY=-166.43 CenterZ=0 NormalX=0 NormalY=0 NormalZ=1 AngleXU=0 Radius=3.26661
    g25: Circle CenterX=-33.5518 CenterY=-176.44 CenterZ=0 NormalX=0 NormalY=0 NormalZ=1 AngleXU=0 Radius=5.64388
    g26: Circle CenterX=-47.2366 CenterY=-173.859 CenterZ=0 NormalX=0 NormalY=0 NormalZ=1 AngleXU=0 Radius=3.01653
    g27: Circle CenterX=-56.2595 CenterY=-171.456 CenterZ=0 NormalX=0 NormalY=0 NormalZ=1 AngleXU=0 Radius=2.12826
    g28: ArcOfCircle CenterX=51.2151 CenterY=-198.473 CenterZ=0 NormalX=0 NormalY=0 NormalZ=1 AngleXU=0 Radius=20 StartAngle=2.78189 EndAngle=4.35269
    g29: LineSegment StartX=32.4951 StartY=-191.433 StartZ=0 EndX=94.6578 EndY=-26.1352 EndZ=0
    g30: LineSegment StartX=43.1192 StartY=-220.001 StartZ=0 EndX=-196.497 EndY=-129.89 EndZ=0
    g31: LineSegment StartX=43.1192 StartY=-220.001 StartZ=0 EndX=44.1752 EndY=-217.193 EndZ=0
    g32: LineSegment StartX=117.223 StartY=-19.0875 StartZ=0 EndX=117.223 EndY=-16.0875 EndZ=0
    g33: LineSegment StartX=117.223 StartY=-16.0875 StartZ=0 EndX=17.2232 EndY=-16.0875 EndZ=0
    g34: LineSegment StartX=17.2232 StartY=-16.0875 StartZ=0 EndX=17.2232 EndY=-19.0875 EndZ=0
    g35: LineSegment StartX=28.8094 StartY=-19.0875 StartZ=0 EndX=17.2232 EndY=-19.0875 EndZ=0
    g36: LineSegment StartX=47.0443 StartY=-50.4712 StartZ=0 EndX=12.8789 EndY=-141.321 EndZ=0
    g37: LineSegment StartX=-195.441 StartY=-127.082 StartZ=0 EndX=-196.497 EndY=-129.89 EndZ=0
    g38: LineSegment StartX=85.2866 StartY=-36.8766 StartZ=0 EndX=78.9396 EndY=-53.7463 EndZ=0
    g39: LineSegment StartX=60.9579 StartY=-27.7053 StartZ=0 EndX=54.6191 EndY=-44.5532 EndZ=0
    g40: LineSegment StartX=68.0907 StartY=-82.7664 StartZ=0 EndX=61.7465 EndY=-99.6365 EndZ=0
    g41: LineSegment StartX=43.7619 StartY=-73.595 StartZ=0 EndX=37.426 EndY=-90.4435 EndZ=0
    g42: LineSegment StartX=50.885 StartY=-128.652 StartZ=0 EndX=44.5456 EndY=-145.522 EndZ=0
    g43: LineSegment StartX=26.5562 StartY=-119.481 StartZ=0 EndX=20.2251 EndY=-136.329 EndZ=0
    g44: LineSegment StartX=9.3071 StartY=-165.349 StartZ=0 EndX=2.97115 EndY=-182.197 EndZ=0
    g45: LineSegment StartX=33.6358 StartY=-174.52 StartZ=0 EndX=27.2917 EndY=-191.39 EndZ=0
  constraints (71):
    c: Block(g0)
    c: Block(g1)
    c: Block(g2)
    c: Block(g4)
    c: Block(g3)
    c: Block(g6)
    c: Block(g5)
    c: Block(g8)
    c: Block(g7)
    c: Weight(g9) = 1
    c: Equal(g9,g10)
    c: Equal(g9,g11)
    c: Equal(g9,g12)
    c: InternalAlignment(g9-g12 -> g13) x4
    c: InternalAlignment(g14,g13)
    c: InternalAlignment(g15,g13)
    c: Block(g16)
    c: Weight(g17) = 1
    c: Equal(g17,g18)
    c: Equal(g17,g19)
    c: InternalAlignment(g17,g20)
    c: InternalAlignment(g18,g20)
    c: InternalAlignment(g19,g20)
    c: InternalAlignment(g21,g20)
    c: InternalAlignment(g22,g20)
    c: Block(g20)
    c: Block(g23)
    c: Block(g24)
    c: Block(g25)
    c: Block(g26)
    c: Block(g27)
    c: Block(g28)
    c: Coincident(g29,g28)
    c: Coincident(g29,g0)
    c: Block(g13)
    c: Coincident(g31,g30)
    c: Coincident(g31,g28)
    c: Block(g31)
    c: Coincident(g32,g0)
    c: Vertical(g32)
    c: Coincident(g33,g32)
    c: Horizontal(g33)
    c: Coincident(g34,g33)
    c: Vertical(g34)
    c: Block(g33)
    c: Coincident(g35,g13)
    c: Coincident(g35,g34)
    c: Horizontal(g35)
    c: Coincident(g36,g13)
    c: Coincident(g36,g20)
    c: Coincident(g37,g20)
    c: Coincident(g37,g30)
    c: Block(g30)
    c: Coincident(g38,g1)
    c: Coincident(g38,g2)
    c: Coincident(g39,g1)
    c: Coincident(g39,g2)
    c: Coincident(g40,g3)
    c: Coincident(g40,g4)
    c: Coincident(g41,g3)
    c: Coincident(g41,g4)
    c: Coincident(g42,g5)
    c: Coincident(g42,g6)
    c: Coincident(g43,g5)
    c: Coincident(g43,g6)
    c: Coincident(g44,g7)
    c: Coincident(g44,g8)
    c: Coincident(g45,g7)
    c: Coincident(g45,g8)
    c: Distance(g30) = 256
    c: Distance(g33) = 100
FEATURE [Part::Extrusion] Extrude002
  Base = -> Sketch001
  Dir = (1,0,0)
  DirMode = 2
  FaceMakerClass = Part::FaceMakerBullseye
  LengthFwd = 8
  LengthRev = 0
  Solid = true
  Symmetric = false
FEATURE [Sketcher::SketchObject] Sketch002
  FullyConstrained = true
  sketch-geometry (20):
    g0: LineSegment StartX=-2.77179 StartY=-200.304 StartZ=0 EndX=5.22821 EndY=-200.304 EndZ=0
    g1: LineSegment StartX=5.22821 StartY=-200.304 StartZ=0 EndX=5.22821 EndY=-197.304 EndZ=0
    g2: LineSegment StartX=-2.77179 StartY=-200.304 StartZ=0 EndX=-2.77179 EndY=-197.304 EndZ=0
    g3: LineSegment StartX=5.22821 StartY=-197.304 StartZ=0 EndX=8.22821 EndY=-197.304 EndZ=0
    g4: LineSegment StartX=-2.77179 StartY=-197.304 StartZ=0 EndX=-5.77179 EndY=-197.304 EndZ=0
    g5: LineSegment StartX=19.2282 StartY=-203.304 StartZ=0 EndX=19.2282 EndY=-206.304 EndZ=0
    g6: LineSegment StartX=-16.7718 StartY=-203.304 StartZ=0 EndX=-16.7718 EndY=-206.304 EndZ=0
    g7: LineSegment StartX=-16.7718 StartY=-206.304 StartZ=0 EndX=19.2282 EndY=-206.304 EndZ=0
    g8: Circle CenterX=-16.7718 CenterY=-203.304 CenterZ=0 NormalX=0 NormalY=0 NormalZ=1 AngleXU=0 Radius=1
    g9: Circle CenterX=-5.77179 CenterY=-203.304 CenterZ=0 NormalX=0 NormalY=0 NormalZ=1 AngleXU=0 Radius=1
    g10: Circle CenterX=-5.77179 CenterY=-197.304 CenterZ=0 NormalX=0 NormalY=0 NormalZ=1 AngleXU=0 Radius=1
    g11: BSplineCurve PolesCount=3 KnotsCount=2 Degree=2 IsPeriodic=0
    g12: GeomPoint X=-16.7718 Y=-203.304 Z=0
    g13: GeomPoint X=-5.77179 Y=-197.304 Z=0
    g14: Circle CenterX=19.2282 CenterY=-203.304 CenterZ=0 NormalX=0 NormalY=0 NormalZ=1 AngleXU=0 Radius=1
    g15: Circle CenterX=8.22821 CenterY=-203.304 CenterZ=0 NormalX=0 NormalY=0 NormalZ=1 AngleXU=0 Radius=1
    g16: Circle CenterX=8.22821 CenterY=-197.304 CenterZ=0 NormalX=0 NormalY=0 NormalZ=1 AngleXU=0 Radius=1
    g17: BSplineCurve PolesCount=3 KnotsCount=2 Degree=2 IsPeriodic=0
    g18: GeomPoint X=19.2282 Y=-203.304 Z=0
    g19: GeomPoint X=8.22821 Y=-197.304 Z=0
  constraints (41):
    c: Horizontal(g0)
    c: Distance(g0) = 8
    c: Coincident(g1,g0)
    c: Vertical(g1)
    c: Distance(g1) = 3
    c: Coincident(g2,g0)
    c: Vertical(g2)
    c: Distance(g2) = 3
    c: Coincident(g3,g1)
    c: Horizontal(g3)
    c: Distance(g3) = 3
    c: Coincident(g4,g2)
    c: Horizontal(g4)
    c: Distance(g4) = 3
    c: Vertical(g5)
    c: Vertical(g6)
    c: Coincident(g7,g6)
    c: Coincident(g7,g5)
    c: Weight(g8) = 1
    c: Equal(g8,g9)
    c: Equal(g8,g10)
    c: Coincident(g11,g4)
    c: InternalAlignment(g8,g11)
    c: InternalAlignment(g9,g11)
    c: InternalAlignment(g10,g11)
    c: InternalAlignment(g12,g11)
    c: InternalAlignment(g13,g11)
    c: Coincident(g17,g5)
    c: Weight(g14) = 1
    c: Equal(g14,g15)
    c: Equal(g14,g16)
    c: Coincident(g17,g3)
    c: InternalAlignment(g14,g17)
    c: InternalAlignment(g15,g17)
    c: InternalAlignment(g16,g17)
    c: InternalAlignment(g18,g17)
    c: InternalAlignment(g19,g17)
    c: Block(g7)
    c: Block(g17)
    c: Block(g11)
    c: Block(g6)
FEATURE [Part::Extrusion] Extrude003
  Base = -> Sketch002
  Dir = (0,0,1)
  DirMode = 2
  FaceMakerClass = Part::FaceMakerBullseye
  LengthFwd = 260
  LengthRev = 0
  Solid = true
  Symmetric = false
FEATURE [Sketcher::SketchObject] Sketch003
  FullyConstrained = false
  sketch-geometry (384):
    g0: LineSegment StartX=-42.9272 StartY=136.221 StartZ=0 EndX=-42.9272 EndY=-103.779 EndZ=0
    g1: LineSegment StartX=407.073 StartY=136.221 StartZ=0 EndX=407.073 EndY=-103.779 EndZ=0
    g2: ArcOfCircle CenterX=-26.9272 CenterY=-83.7794 CenterZ=0 NormalX=0 NormalY=0 NormalZ=1 AngleXU=0 Radius=8 StartAngle=3.14159 EndAngle=6.28319
    g3: ArcOfCircle CenterX=391.073 CenterY=-83.7794 CenterZ=0 NormalX=0 NormalY=0 NormalZ=1 AngleXU=0 Radius=8 StartAngle=3.14159 EndAngle=6.28319
    g4: Circle CenterX=175.022 CenterY=27.0628 CenterZ=0 NormalX=0 NormalY=0 NormalZ=1 AngleXU=0 Radius=1
    g5: Circle CenterX=179.022 CenterY=24.8665 CenterZ=0 NormalX=0 NormalY=0 NormalZ=1 AngleXU=0 Radius=1
    g6: Circle CenterX=179.022 CenterY=27.0628 CenterZ=0 NormalX=0 NormalY=0 NormalZ=1 AngleXU=0 Radius=1
    g7: BSplineCurve PolesCount=3 KnotsCount=2 Degree=2 IsPeriodic=0
    g8: GeomPoint X=175.022 Y=27.0628 Z=0
    g9: GeomPoint X=179.022 Y=27.0628 Z=0
    g10: Circle CenterX=189.124 CenterY=27.0628 CenterZ=0 NormalX=0 NormalY=0 NormalZ=1 AngleXU=0 Radius=1
    g11: Circle CenterX=185.124 CenterY=24.8665 CenterZ=0 NormalX=0 NormalY=0 NormalZ=1 AngleXU=0 Radius=1
    g12: Circle CenterX=185.124 CenterY=27.0628 CenterZ=0 NormalX=0 NormalY=0 NormalZ=1 AngleXU=0 Radius=1
    g13: BSplineCurve PolesCount=3 KnotsCount=2 Degree=2 IsPeriodic=0
    g14: GeomPoint X=189.124 Y=27.0628 Z=0
    g15: GeomPoint X=185.124 Y=27.0628 Z=0
    g16: Circle CenterX=175.022 CenterY=5.37834 CenterZ=0 NormalX=0 NormalY=0 NormalZ=1 AngleXU=0 Radius=1
    g17: Circle CenterX=179.022 CenterY=7.57463 CenterZ=0 NormalX=0 NormalY=0 NormalZ=1 AngleXU=0 Radius=1
    g18: Circle CenterX=179.022 CenterY=5.34704 CenterZ=0 NormalX=0 NormalY=0 NormalZ=1 AngleXU=0 Radius=1
    g19: BSplineCurve PolesCount=3 KnotsCount=2 Degree=2 IsPeriodic=0
    g20: GeomPoint X=175.022 Y=5.37834 Z=0
    g21: GeomPoint X=179.022 Y=5.34704 Z=0
    g22: Circle CenterX=189.124 CenterY=5.37834 CenterZ=0 NormalX=0 NormalY=0 NormalZ=1 AngleXU=0 Radius=1
    g23: Circle CenterX=185.124 CenterY=7.57463 CenterZ=0 NormalX=0 NormalY=0 NormalZ=1 AngleXU=0 Radius=1
    g24: Circle CenterX=185.124 CenterY=5.34704 CenterZ=0 NormalX=0 NormalY=0 NormalZ=1 AngleXU=0 Radius=1
    g25: BSplineCurve PolesCount=3 KnotsCount=2 Degree=2 IsPeriodic=0
    g26: GeomPoint X=189.124 Y=5.37834 Z=0
    g27: GeomPoint X=185.124 Y=5.34704 Z=0
    g28: Circle CenterX=165.871 CenterY=18.1458 CenterZ=0 NormalX=0 NormalY=0 NormalZ=1 AngleXU=0 Radius=1
    g29: Circle CenterX=169.377 CenterY=16.2206 CenterZ=0 NormalX=0 NormalY=0 NormalZ=1 AngleXU=0 Radius=1
    g30: Circle CenterX=165.871 CenterY=14.2954 CenterZ=0 NormalX=0 NormalY=0 NormalZ=1 AngleXU=0 Radius=1
    g31: BSplineCurve PolesCount=3 KnotsCount=2 Degree=2 IsPeriodic=0
    g32: GeomPoint X=165.871 Y=18.1458 Z=0
    g33: GeomPoint X=165.871 Y=14.2954 Z=0
    g34: Circle CenterX=198.275 CenterY=18.1458 CenterZ=0 NormalX=0 NormalY=0 NormalZ=1 AngleXU=0 Radius=1
    g35: Circle CenterX=194.768 CenterY=16.2206 CenterZ=0 NormalX=0 NormalY=0 NormalZ=1 AngleXU=0 Radius=1
    g36: Circle CenterX=198.275 CenterY=14.2954 CenterZ=0 NormalX=0 NormalY=0 NormalZ=1 AngleXU=0 Radius=1
    g37: BSplineCurve PolesCount=3 KnotsCount=2 Degree=2 IsPeriodic=0
    g38: GeomPoint X=198.275 Y=18.1458 Z=0
    g39: GeomPoint X=198.275 Y=14.2954 Z=0
    g40: LineSegment StartX=407.073 StartY=-103.779 StartZ=0 EndX=-42.9272 EndY=-103.779 EndZ=0
    g41: Circle CenterX=125.607 CenterY=54.1951 CenterZ=0 NormalX=0 NormalY=0 NormalZ=1 AngleXU=0 Radius=1
    g42: Circle CenterX=139.632 CenterY=46.4944 CenterZ=0 NormalX=0 NormalY=0 NormalZ=1 AngleXU=0 Radius=1
    g43: Circle CenterX=127.326 CenterY=56.7187 CenterZ=0 NormalX=0 NormalY=0 NormalZ=1 AngleXU=0 Radius=1
    g44: BSplineCurve PolesCount=3 KnotsCount=2 Degree=2 IsPeriodic=0
    g45: GeomPoint X=125.607 Y=54.1951 Z=0
    g46: GeomPoint X=127.326 Y=56.7187 Z=0
    g47: Circle CenterX=236.821 CenterY=56.7187 CenterZ=0 NormalX=0 NormalY=0 NormalZ=1 AngleXU=0 Radius=1
    g48: Circle CenterX=224.513 CenterY=46.4944 CenterZ=0 NormalX=0 NormalY=0 NormalZ=1 AngleXU=0 Radius=1
    g49: Circle CenterX=238.538 CenterY=54.1951 CenterZ=0 NormalX=0 NormalY=0 NormalZ=1 AngleXU=0 Radius=1
    g50: BSplineCurve PolesCount=3 KnotsCount=2 Degree=2 IsPeriodic=0
    g51: GeomPoint X=236.821 Y=56.7187 Z=0
    g52: GeomPoint X=238.538 Y=54.1951 Z=0
    g53: Circle CenterX=238.538 CenterY=-21.7539 CenterZ=0 NormalX=0 NormalY=0 NormalZ=1 AngleXU=0 Radius=1
    g54: Circle CenterX=224.513 CenterY=-14.0532 CenterZ=0 NormalX=0 NormalY=0 NormalZ=1 AngleXU=0 Radius=1
    g55: Circle CenterX=236.821 CenterY=-24.2775 CenterZ=0 NormalX=0 NormalY=0 NormalZ=1 AngleXU=0 Radius=1
    g56: BSplineCurve PolesCount=3 KnotsCount=2 Degree=2 IsPeriodic=0
    g57: GeomPoint X=238.538 Y=-21.7539 Z=0
    g58: GeomPoint X=236.821 Y=-24.2775 Z=0
    g59: Circle CenterX=125.607 CenterY=-21.7539 CenterZ=0 NormalX=0 NormalY=0 NormalZ=1 AngleXU=0 Radius=1
    g60: Circle CenterX=139.632 CenterY=-14.0532 CenterZ=0 NormalX=0 NormalY=0 NormalZ=1 AngleXU=0 Radius=1
    g61: Circle CenterX=127.325 CenterY=-24.2775 CenterZ=0 NormalX=0 NormalY=0 NormalZ=1 AngleXU=0 Radius=1
    g62: BSplineCurve PolesCount=3 KnotsCount=2 Degree=2 IsPeriodic=0
    g63: GeomPoint X=125.607 Y=-21.7539 Z=0
    g64: GeomPoint X=127.325 Y=-24.2775 Z=0
    g65: Circle CenterX=302.996 CenterY=111.695 CenterZ=0 NormalX=0 NormalY=0 NormalZ=1 AngleXU=0 Radius=1
    g66: Circle CenterX=306.073 CenterY=114.251 CenterZ=0 NormalX=0 NormalY=0 NormalZ=1 AngleXU=0 Radius=1
    g67: Circle CenterX=306.073 CenterY=110.251 CenterZ=0 NormalX=0 NormalY=0 NormalZ=1 AngleXU=0 Radius=1
    g68: BSplineCurve PolesCount=3 KnotsCount=2 Degree=2 IsPeriodic=0
    g69: GeomPoint X=302.996 Y=111.695 Z=0
    g70: GeomPoint X=306.073 Y=110.251 Z=0
    g71: Circle CenterX=306.073 CenterY=95.2763 CenterZ=0 NormalX=0 NormalY=0 NormalZ=1 AngleXU=0 Radius=1
    g72: Circle CenterX=306.073 CenterY=91.2763 CenterZ=0 NormalX=0 NormalY=0 NormalZ=1 AngleXU=0 Radius=1
    g73: Circle CenterX=302.567 CenterY=89.3511 CenterZ=0 NormalX=0 NormalY=0 NormalZ=1 AngleXU=0 Radius=1
    g74: BSplineCurve PolesCount=3 KnotsCount=2 Degree=2 IsPeriodic=0
    g75: GeomPoint X=306.073 Y=95.2763 Z=0
    g76: GeomPoint X=302.567 Y=89.3511 Z=0
    g77: LineSegment StartX=306.073 StartY=110.251 StartZ=0 EndX=306.073 EndY=95.2763 EndZ=0
    g78: LineSegment StartX=302.996 StartY=111.695 StartZ=0 EndX=236.821 EndY=56.7187 EndZ=0
    g79: LineSegment StartX=238.538 StartY=54.1951 StartZ=0 EndX=302.567 EndY=89.3511 EndZ=0
    g80: Circle CenterX=61.1496 CenterY=111.695 CenterZ=0 NormalX=0 NormalY=0 NormalZ=1 AngleXU=0 Radius=1
    g81: Circle CenterX=58.0728 CenterY=114.251 CenterZ=0 NormalX=0 NormalY=0 NormalZ=1 AngleXU=0 Radius=1
    g82: Circle CenterX=58.0728 CenterY=110.251 CenterZ=0 NormalX=0 NormalY=0 NormalZ=1 AngleXU=0 Radius=1
    g83: BSplineCurve PolesCount=3 KnotsCount=2 Degree=2 IsPeriodic=0
    g84: GeomPoint X=61.1496 Y=111.695 Z=0
    g85: GeomPoint X=58.0728 Y=110.251 Z=0
    g86: Circle CenterX=61.5791 CenterY=89.3511 CenterZ=0 NormalX=0 NormalY=0 NormalZ=1 AngleXU=0 Radius=1
    g87: Circle CenterX=58.0728 CenterY=91.2763 CenterZ=0 NormalX=0 NormalY=0 NormalZ=1 AngleXU=0 Radius=1
    g88: Circle CenterX=58.0728 CenterY=95.2763 CenterZ=0 NormalX=0 NormalY=0 NormalZ=1 AngleXU=0 Radius=1
    g89: BSplineCurve PolesCount=3 KnotsCount=2 Degree=2 IsPeriodic=0
    g90: GeomPoint X=61.5791 Y=89.3511 Z=0
    g91: GeomPoint X=58.0728 Y=95.2763 Z=0
    g92: LineSegment StartX=58.0728 StartY=110.251 StartZ=0 EndX=58.0728 EndY=95.2763 EndZ=0
    g93: LineSegment StartX=61.1496 StartY=111.695 StartZ=0 EndX=127.326 EndY=56.7187 EndZ=0
    g94: LineSegment StartX=125.607 StartY=54.1951 StartZ=0 EndX=61.5791 EndY=89.3511 EndZ=0
    g95: Circle CenterX=61.5791 CenterY=-56.9099 CenterZ=0 NormalX=0 NormalY=0 NormalZ=1 AngleXU=0 Radius=1
    g96: Circle CenterX=58.0728 CenterY=-58.8351 CenterZ=0 NormalX=0 NormalY=0 NormalZ=1 AngleXU=0 Radius=1
    g97: Circle CenterX=58.0728 CenterY=-62.8351 CenterZ=0 NormalX=0 NormalY=0 NormalZ=1 AngleXU=0 Radius=1
    g98: BSplineCurve PolesCount=3 KnotsCount=2 Degree=2 IsPeriodic=0
    g99: GeomPoint X=61.5791 Y=-56.9099 Z=0
    g100: GeomPoint X=58.0728 Y=-62.8351 Z=0
    g101: Circle CenterX=58.0728 CenterY=-77.8102 CenterZ=0 NormalX=0 NormalY=0 NormalZ=1 AngleXU=0 Radius=1
    g102: Circle CenterX=58.0728 CenterY=-81.8102 CenterZ=0 NormalX=0 NormalY=0 NormalZ=1 AngleXU=0 Radius=1
    g103: Circle CenterX=61.1496 CenterY=-79.2541 CenterZ=0 NormalX=0 NormalY=0 NormalZ=1 AngleXU=0 Radius=1
    g104: BSplineCurve PolesCount=3 KnotsCount=2 Degree=2 IsPeriodic=0
    g105: GeomPoint X=58.0728 Y=-77.8102 Z=0
    g106: GeomPoint X=61.1496 Y=-79.2541 Z=0
    g107: LineSegment StartX=58.0728 StartY=-62.8351 StartZ=0 EndX=58.0728 EndY=-77.8102 EndZ=0
    g108: LineSegment StartX=61.1496 StartY=-79.2541 StartZ=0 EndX=127.325 EndY=-24.2775 EndZ=0
    g109: LineSegment StartX=125.607 StartY=-21.7539 StartZ=0 EndX=61.5791 EndY=-56.9099 EndZ=0
    g110: Circle CenterX=302.567 CenterY=-56.9099 CenterZ=0 NormalX=0 NormalY=0 NormalZ=1 AngleXU=0 Radius=1
    g111: Circle CenterX=306.073 CenterY=-58.8351 CenterZ=0 NormalX=0 NormalY=0 NormalZ=1 AngleXU=0 Radius=1
    g112: Circle CenterX=306.073 CenterY=-62.8351 CenterZ=0 NormalX=0 NormalY=0 NormalZ=1 AngleXU=0 Radius=1
    g113: BSplineCurve PolesCount=3 KnotsCount=2 Degree=2 IsPeriodic=0
    g114: GeomPoint X=302.567 Y=-56.9099 Z=0
    g115: GeomPoint X=306.073 Y=-62.8351 Z=0
    g116: Circle CenterX=302.996 CenterY=-79.2541 CenterZ=0 NormalX=0 NormalY=0 NormalZ=1 AngleXU=0 Radius=1
    g117: Circle CenterX=306.073 CenterY=-81.8102 CenterZ=0 NormalX=0 NormalY=0 NormalZ=1 AngleXU=0 Radius=1
    g118: Circle CenterX=306.073 CenterY=-77.8102 CenterZ=0 NormalX=0 NormalY=0 NormalZ=1 AngleXU=0 Radius=1
    g119: BSplineCurve PolesCount=3 KnotsCount=2 Degree=2 IsPeriodic=0
    g120: GeomPoint X=302.996 Y=-79.2541 Z=0
    g121: GeomPoint X=306.073 Y=-77.8102 Z=0
    g122: LineSegment StartX=306.073 StartY=-62.8351 StartZ=0 EndX=306.073 EndY=-77.8102 EndZ=0
    g123: LineSegment StartX=302.996 StartY=-79.2541 StartZ=0 EndX=236.821 EndY=-24.2775 EndZ=0
    g124: LineSegment StartX=238.538 StartY=-21.7539 StartZ=0 EndX=302.567 EndY=-56.9099 EndZ=0
    g125: Circle CenterX=61.6457 CenterY=-88.8112 CenterZ=0 NormalX=0 NormalY=0 NormalZ=1 AngleXU=0 Radius=1
    g126: Circle CenterX=58.0728 CenterY=-91.7794 CenterZ=0 NormalX=0 NormalY=0 NormalZ=1 AngleXU=0 Radius=1
    g127: Circle CenterX=63.9135 CenterY=-91.7794 CenterZ=0 NormalX=0 NormalY=0 NormalZ=1 AngleXU=0 Radius=1
    g128: BSplineCurve PolesCount=3 KnotsCount=2 Degree=2 IsPeriodic=0
    g129: GeomPoint X=61.6457 Y=-88.8112 Z=0
    g130: GeomPoint X=63.9135 Y=-91.7794 Z=0
    g131: Circle CenterX=179.022 CenterY=-85.8163 CenterZ=0 NormalX=0 NormalY=0 NormalZ=1 AngleXU=0 Radius=1
    g132: Circle CenterX=179.022 CenterY=-91.7794 CenterZ=0 NormalX=0 NormalY=0 NormalZ=1 AngleXU=0 Radius=1
    g133: Circle CenterX=171.895 CenterY=-91.7794 CenterZ=0 NormalX=0 NormalY=0 NormalZ=1 AngleXU=0 Radius=1
    g134: BSplineCurve PolesCount=3 KnotsCount=2 Degree=2 IsPeriodic=0
    g135: GeomPoint X=179.022 Y=-85.8163 Z=0
    g136: GeomPoint X=171.895 Y=-91.7794 Z=0
    g137: Circle CenterX=185.124 CenterY=-86.2028 CenterZ=0 NormalX=0 NormalY=0 NormalZ=1 AngleXU=0 Radius=1
    g138: Circle CenterX=185.124 CenterY=-91.7794 CenterZ=0 NormalX=0 NormalY=0 NormalZ=1 AngleXU=0 Radius=1
    g139: Circle CenterX=191.747 CenterY=-91.7794 CenterZ=0 NormalX=0 NormalY=0 NormalZ=1 AngleXU=0 Radius=1
    g140: BSplineCurve PolesCount=3 KnotsCount=2 Degree=2 IsPeriodic=0
    g141: GeomPoint X=185.124 Y=-86.2028 Z=0
    g142: GeomPoint X=191.747 Y=-91.7794 Z=0
    g143: Circle CenterX=299.888 CenterY=-86.6413 CenterZ=0 NormalX=0 NormalY=0 NormalZ=1 AngleXU=0 Radius=1
    g144: Circle CenterX=306.073 CenterY=-91.7794 CenterZ=0 NormalX=0 NormalY=0 NormalZ=1 AngleXU=0 Radius=1
    g145: Circle CenterX=298.776 CenterY=-91.7794 CenterZ=0 NormalX=0 NormalY=0 NormalZ=1 AngleXU=0 Radius=1
    g146: BSplineCurve PolesCount=3 KnotsCount=2 Degree=2 IsPeriodic=0
    g147: GeomPoint X=299.888 Y=-86.6413 Z=0
    g148: GeomPoint X=298.776 Y=-91.7794 Z=0
    g149: LineSegment StartX=189.124 StartY=5.37834 StartZ=0 EndX=299.888 EndY=-86.6413 EndZ=0
    g150: LineSegment StartX=298.776 StartY=-91.7794 StartZ=0 EndX=191.747 EndY=-91.7794 EndZ=0
    g151: LineSegment StartX=185.124 StartY=-86.2028 StartZ=0 EndX=185.124 EndY=5.34704 EndZ=0
    g152: LineSegment StartX=179.022 StartY=5.34704 StartZ=0 EndX=179.022 EndY=-85.8163 EndZ=0
    g153: LineSegment StartX=171.895 StartY=-91.7794 StartZ=0 EndX=63.9135 EndY=-91.7794 EndZ=0
    g154: LineSegment StartX=61.6457 StartY=-88.8112 StartZ=0 EndX=175.022 EndY=5.37834 EndZ=0
    g155: Circle CenterX=302.073 CenterY=124.221 CenterZ=0 NormalX=0 NormalY=0 NormalZ=1 AngleXU=0 Radius=1
    g156: Circle CenterX=306.073 CenterY=124.221 CenterZ=0 NormalX=0 NormalY=0 NormalZ=1 AngleXU=0 Radius=1
    g157: Circle CenterX=302.996 CenterY=121.665 CenterZ=0 NormalX=0 NormalY=0 NormalZ=1 AngleXU=0 Radius=1
    g158: BSplineCurve PolesCount=3 KnotsCount=2 Degree=2 IsPeriodic=0
    g159: GeomPoint X=302.073 Y=124.221 Z=0
    g160: GeomPoint X=302.996 Y=121.665 Z=0
    g161: Circle CenterX=189.124 CenterY=124.221 CenterZ=0 NormalX=0 NormalY=0 NormalZ=1 AngleXU=0 Radius=1
    g162: Circle CenterX=185.124 CenterY=124.221 CenterZ=0 NormalX=0 NormalY=0 NormalZ=1 AngleXU=0 Radius=1
    g163: Circle CenterX=185.124 CenterY=120.221 CenterZ=0 NormalX=0 NormalY=0 NormalZ=1 AngleXU=0 Radius=1
    g164: BSplineCurve PolesCount=3 KnotsCount=2 Degree=2 IsPeriodic=0
    g165: GeomPoint X=189.124 Y=124.221 Z=0
    g166: GeomPoint X=185.124 Y=120.221 Z=0
    g167: Circle CenterX=175.022 CenterY=124.221 CenterZ=0 NormalX=0 NormalY=0 NormalZ=1 AngleXU=0 Radius=1
    g168: Circle CenterX=179.022 CenterY=124.221 CenterZ=0 NormalX=0 NormalY=0 NormalZ=1 AngleXU=0 Radius=1
    g169: Circle CenterX=179.022 CenterY=120.221 CenterZ=0 NormalX=0 NormalY=0 NormalZ=1 AngleXU=0 Radius=1
    g170: BSplineCurve PolesCount=3 KnotsCount=2 Degree=2 IsPeriodic=0
    g171: GeomPoint X=175.022 Y=124.221 Z=0
    g172: GeomPoint X=179.022 Y=120.221 Z=0
    g173: Circle CenterX=62.0728 CenterY=124.221 CenterZ=0 NormalX=0 NormalY=0 NormalZ=1 AngleXU=0 Radius=1
    g174: Circle CenterX=58.0728 CenterY=124.221 CenterZ=0 NormalX=0 NormalY=0 NormalZ=1 AngleXU=0 Radius=1
    g175: Circle CenterX=61.1496 CenterY=121.665 CenterZ=0 NormalX=0 NormalY=0 NormalZ=1 AngleXU=0 Radius=1
    g176: BSplineCurve PolesCount=3 KnotsCount=2 Degree=2 IsPeriodic=0
    g177: GeomPoint X=62.0728 Y=124.221 Z=0
    g178: GeomPoint X=61.1496 Y=121.665 Z=0
    g179: LineSegment StartX=62.0728 StartY=124.221 StartZ=0 EndX=175.022 EndY=124.221 EndZ=0
    g180: LineSegment StartX=179.022 StartY=120.221 StartZ=0 EndX=179.022 EndY=27.0628 EndZ=0
    g181: LineSegment StartX=185.124 StartY=27.0628 StartZ=0 EndX=185.124 EndY=120.221 EndZ=0
    g182: LineSegment StartX=302.996 StartY=121.665 StartZ=0 EndX=189.124 EndY=27.0628 EndZ=0
    g183: LineSegment StartX=175.022 StartY=27.0628 StartZ=0 EndX=61.1496 EndY=121.665 EndZ=0
    g184: Circle CenterX=61.5791 CenterY=75.4095 CenterZ=0 NormalX=0 NormalY=0 NormalZ=1 AngleXU=0 Radius=1
    g185: Circle CenterX=58.0728 CenterY=77.3346 CenterZ=0 NormalX=0 NormalY=0 NormalZ=1 AngleXU=0 Radius=1
    g186: Circle CenterX=58.0728 CenterY=73.3346 CenterZ=0 NormalX=0 NormalY=0 NormalZ=1 AngleXU=0 Radius=1
    g187: BSplineCurve PolesCount=3 KnotsCount=2 Degree=2 IsPeriodic=0
    g188: GeomPoint X=61.5791 Y=75.4095 Z=0
    g189: GeomPoint X=58.0728 Y=73.3346 Z=0
    g190: Circle CenterX=58.0728 CenterY=-40.8935 CenterZ=0 NormalX=0 NormalY=0 NormalZ=1 AngleXU=0 Radius=1
    g191: Circle CenterX=58.0728 CenterY=-44.8935 CenterZ=0 NormalX=0 NormalY=0 NormalZ=1 AngleXU=0 Radius=1
    g192: Circle CenterX=61.5791 CenterY=-42.9683 CenterZ=0 NormalX=0 NormalY=0 NormalZ=1 AngleXU=0 Radius=1
    g193: BSplineCurve PolesCount=3 KnotsCount=2 Degree=2 IsPeriodic=0
    g194: GeomPoint X=58.0728 Y=-40.8935 Z=0
    g195: GeomPoint X=61.5791 Y=-42.9683 Z=0
    g196: LineSegment StartX=61.5791 StartY=-42.9683 StartZ=0 EndX=165.871 EndY=14.2954 EndZ=0
    g197: LineSegment StartX=165.871 StartY=18.1458 StartZ=0 EndX=61.5791 EndY=75.4095 EndZ=0
    g198: LineSegment StartX=58.0728 StartY=73.3346 StartZ=0 EndX=58.0728 EndY=-40.8935 EndZ=0
    g199: Circle CenterX=302.567 CenterY=-42.9683 CenterZ=0 NormalX=0 NormalY=0 NormalZ=1 AngleXU=0 Radius=1
    g200: Circle CenterX=306.073 CenterY=-44.8935 CenterZ=0 NormalX=0 NormalY=0 NormalZ=1 AngleXU=0 Radius=1
    g201: Circle CenterX=306.073 CenterY=-40.8935 CenterZ=0 NormalX=0 NormalY=0 NormalZ=1 AngleXU=0 Radius=1
    g202: BSplineCurve PolesCount=3 KnotsCount=2 Degree=2 IsPeriodic=0
    g203: GeomPoint X=302.567 Y=-42.9683 Z=0
    g204: GeomPoint X=306.073 Y=-40.8935 Z=0
    g205: Circle CenterX=306.073 CenterY=73.3346 CenterZ=0 NormalX=0 NormalY=0 NormalZ=1 AngleXU=0 Radius=1
    g206: Circle CenterX=306.073 CenterY=77.3346 CenterZ=0 NormalX=0 NormalY=0 NormalZ=1 AngleXU=0 Radius=1
    g207: Circle CenterX=302.567 CenterY=75.4095 CenterZ=0 NormalX=0 NormalY=0 NormalZ=1 AngleXU=0 Radius=1
    g208: BSplineCurve PolesCount=3 KnotsCount=2 Degree=2 IsPeriodic=0
    g209: GeomPoint X=306.073 Y=73.3346 Z=0
    g210: GeomPoint X=302.567 Y=75.4095 Z=0
    g211: LineSegment StartX=302.567 StartY=-42.9683 StartZ=0 EndX=198.275 EndY=14.2954 EndZ=0
    g212: LineSegment StartX=198.275 StartY=18.1458 StartZ=0 EndX=302.567 EndY=75.4095 EndZ=0
    g213: LineSegment StartX=306.073 StartY=73.3346 StartZ=0 EndX=306.073 EndY=-40.8935 EndZ=0
    g214: LineSegment StartX=322.073 StartY=105.865 StartZ=0 EndX=328.643 EndY=105.865 EndZ=0
    g215: LineSegment StartX=318.073 StartY=120.221 StartZ=0 EndX=318.073 EndY=109.865 EndZ=0
    g216: LineSegment StartX=336.157 StartY=107.779 StartZ=0 EndX=362.567 EndY=122.294 EndZ=0
    g217: Circle CenterX=362.073 CenterY=124.221 CenterZ=0 NormalX=0 NormalY=0 NormalZ=1 AngleXU=0 Radius=1
    g218: Circle CenterX=366.073 CenterY=124.221 CenterZ=0 NormalX=0 NormalY=0 NormalZ=1 AngleXU=0 Radius=1
    g219: Circle CenterX=362.567 CenterY=122.294 CenterZ=0 NormalX=0 NormalY=0 NormalZ=1 AngleXU=0 Radius=1
    g220: BSplineCurve PolesCount=3 KnotsCount=2 Degree=2 IsPeriodic=0
    g221: GeomPoint X=362.073 Y=124.221 Z=0
    g222: GeomPoint X=362.567 Y=122.294 Z=0
    g223: Circle CenterX=322.073 CenterY=124.221 CenterZ=0 NormalX=0 NormalY=0 NormalZ=1 AngleXU=0 Radius=1
    g224: Circle CenterX=318.073 CenterY=124.221 CenterZ=0 NormalX=0 NormalY=0 NormalZ=1 AngleXU=0 Radius=1
    g225: Circle CenterX=318.073 CenterY=120.221 CenterZ=0 NormalX=0 NormalY=0 NormalZ=1 AngleXU=0 Radius=1
    g226: BSplineCurve PolesCount=3 KnotsCount=2 Degree=2 IsPeriodic=0
    g227: GeomPoint X=322.073 Y=124.221 Z=0
    g228: GeomPoint X=318.073 Y=120.221 Z=0
    g229: Circle CenterX=322.073 CenterY=105.865 CenterZ=0 NormalX=0 NormalY=0 NormalZ=1 AngleXU=0 Radius=1
    g230: Circle CenterX=318.073 CenterY=105.865 CenterZ=0 NormalX=0 NormalY=0 NormalZ=1 AngleXU=0 Radius=1
    g231: Circle CenterX=318.073 CenterY=109.865 CenterZ=0 NormalX=0 NormalY=0 NormalZ=1 AngleXU=0 Radius=1
    g232: BSplineCurve PolesCount=3 KnotsCount=2 Degree=2 IsPeriodic=0
    g233: GeomPoint X=322.073 Y=105.865 Z=0
    g234: GeomPoint X=318.073 Y=109.865 Z=0
    g235: Circle CenterX=336.157 CenterY=107.779 CenterZ=0 NormalX=0 NormalY=0 NormalZ=1 AngleXU=0 Radius=1
    g236: Circle CenterX=332.651 CenterY=105.853 CenterZ=0 NormalX=0 NormalY=0 NormalZ=1 AngleXU=0 Radius=1
    g237: Circle CenterX=328.643 CenterY=105.865 CenterZ=0 NormalX=0 NormalY=0 NormalZ=1 AngleXU=0 Radius=1
    g238: BSplineCurve PolesCount=3 KnotsCount=2 Degree=2 IsPeriodic=0
    g239: GeomPoint X=336.157 Y=107.779 Z=0
    g240: GeomPoint X=328.643 Y=105.865 Z=0
    g241: LineSegment StartX=322.073 StartY=124.221 StartZ=0 EndX=362.073 EndY=124.221 EndZ=0
    g242: Circle CenterX=371.567 CenterY=-80.8644 CenterZ=0 NormalX=0 NormalY=0 NormalZ=1 AngleXU=0 Radius=1
    g243: Circle CenterX=375.073 CenterY=-82.7896 CenterZ=0 NormalX=0 NormalY=0 NormalZ=1 AngleXU=0 Radius=1
    g244: Circle CenterX=375.073 CenterY=-78.7896 CenterZ=0 NormalX=0 NormalY=0 NormalZ=1 AngleXU=0 Radius=1
    g245: BSplineCurve PolesCount=3 KnotsCount=2 Degree=2 IsPeriodic=0
    g246: GeomPoint X=371.567 Y=-80.8644 Z=0
    g247: GeomPoint X=375.073 Y=-78.7896 Z=0
    g248: Circle CenterX=321.579 CenterY=-53.4075 CenterZ=0 NormalX=0 NormalY=0 NormalZ=1 AngleXU=0 Radius=1
    g249: Circle CenterX=318.073 CenterY=-51.4823 CenterZ=0 NormalX=0 NormalY=0 NormalZ=1 AngleXU=0 Radius=1
    g250: Circle CenterX=318.073 CenterY=-47.4805 CenterZ=0 NormalX=0 NormalY=0 NormalZ=1 AngleXU=0 Radius=1
    g251: BSplineCurve PolesCount=3 KnotsCount=2 Degree=2 IsPeriodic=0
    g252: GeomPoint X=321.579 Y=-53.4075 Z=0
    g253: GeomPoint X=318.073 Y=-47.4805 Z=0
    g254: LineSegment StartX=371.567 StartY=-80.8644 StartZ=0 EndX=321.579 EndY=-53.4075 EndZ=0
    g255: Circle CenterX=321.579 CenterY=-67.3492 CenterZ=0 NormalX=0 NormalY=0 NormalZ=1 AngleXU=0 Radius=1
    g256: Circle CenterX=318.073 CenterY=-65.424 CenterZ=0 NormalX=0 NormalY=0 NormalZ=1 AngleXU=0 Radius=1
    g257: Circle CenterX=318.073 CenterY=-69.424 CenterZ=0 NormalX=0 NormalY=0 NormalZ=1 AngleXU=0 Radius=1
    g258: BSplineCurve PolesCount=3 KnotsCount=2 Degree=2 IsPeriodic=0
    g259: GeomPoint X=321.579 Y=-67.3492 Z=0
    g260: GeomPoint X=318.073 Y=-69.424 Z=0
    g261: Circle CenterX=362.567 CenterY=-89.8542 CenterZ=0 NormalX=0 NormalY=0 NormalZ=1 AngleXU=0 Radius=1
    g262: Circle CenterX=366.073 CenterY=-91.7794 CenterZ=0 NormalX=0 NormalY=0 NormalZ=1 AngleXU=0 Radius=1
    g263: Circle CenterX=362.073 CenterY=-91.7794 CenterZ=0 NormalX=0 NormalY=0 NormalZ=1 AngleXU=0 Radius=1
    g264: BSplineCurve PolesCount=3 KnotsCount=2 Degree=2 IsPeriodic=0
    g265: GeomPoint X=362.567 Y=-89.8542 Z=0
    g266: GeomPoint X=362.073 Y=-91.7794 Z=0
    g267: Circle CenterX=322.073 CenterY=-91.7794 CenterZ=0 NormalX=0 NormalY=0 NormalZ=1 AngleXU=0 Radius=1
    g268: Circle CenterX=318.073 CenterY=-91.7794 CenterZ=0 NormalX=0 NormalY=0 NormalZ=1 AngleXU=0 Radius=1
    g269: Circle CenterX=318.073 CenterY=-87.7794 CenterZ=0 NormalX=0 NormalY=0 NormalZ=1 AngleXU=0 Radius=1
    g270: BSplineCurve PolesCount=3 KnotsCount=2 Degree=2 IsPeriodic=0
    g271: GeomPoint X=322.073 Y=-91.7794 Z=0
    g272: GeomPoint X=318.073 Y=-87.7794 Z=0
    g273: LineSegment StartX=362.567 StartY=-89.8542 StartZ=0 EndX=321.579 EndY=-67.3492 EndZ=0
    g274: LineSegment StartX=318.073 StartY=-69.424 StartZ=0 EndX=318.073 EndY=-87.7794 EndZ=0
    g275: LineSegment StartX=322.073 StartY=-91.7794 StartZ=0 EndX=362.073 EndY=-91.7794 EndZ=0
    g276: Circle CenterX=2.07281 CenterY=124.221 CenterZ=0 NormalX=0 NormalY=0 NormalZ=1 AngleXU=0 Radius=1
    g277: Circle CenterX=1.57905 CenterY=122.295 CenterZ=0 NormalX=0 NormalY=0 NormalZ=1 AngleXU=0 Radius=1
    g278: BSplineCurve PolesCount=3 KnotsCount=2 Degree=2 IsPeriodic=0
    g279: GeomPoint X=2.07281 Y=124.221 Z=0
    g280: GeomPoint X=1.57905 Y=122.295 Z=0
    g281: Circle CenterX=42.0728 CenterY=124.221 CenterZ=0 NormalX=0 NormalY=0 NormalZ=1 AngleXU=0 Radius=1
    g282: Circle CenterX=46.0728 CenterY=124.221 CenterZ=0 NormalX=0 NormalY=0 NormalZ=1 AngleXU=0 Radius=1
    g283: Circle CenterX=46.0728 CenterY=120.221 CenterZ=0 NormalX=0 NormalY=0 NormalZ=1 AngleXU=0 Radius=1
    g284: BSplineCurve PolesCount=3 KnotsCount=2 Degree=2 IsPeriodic=0
    g285: GeomPoint X=42.0728 Y=124.221 Z=0
    g286: GeomPoint X=46.0728 Y=120.221 Z=0
    g287: Circle CenterX=46.0728 CenterY=109.865 CenterZ=0 NormalX=0 NormalY=0 NormalZ=1 AngleXU=0 Radius=1
    g288: Circle CenterX=46.0728 CenterY=105.865 CenterZ=0 NormalX=0 NormalY=0 NormalZ=1 AngleXU=0 Radius=1
    g289: Circle CenterX=42.0728 CenterY=105.865 CenterZ=0 NormalX=0 NormalY=0 NormalZ=1 AngleXU=0 Radius=1
    g290: BSplineCurve PolesCount=3 KnotsCount=2 Degree=2 IsPeriodic=0
    g291: GeomPoint X=46.0728 Y=109.865 Z=0
    g292: GeomPoint X=42.0728 Y=105.865 Z=0
    g293: Circle CenterX=35.5028 CenterY=105.865 CenterZ=0 NormalX=0 NormalY=0 NormalZ=1 AngleXU=0 Radius=1
    g294: Circle CenterX=31.5028 CenterY=105.865 CenterZ=0 NormalX=0 NormalY=0 NormalZ=1 AngleXU=0 Radius=1
    g295: Circle CenterX=27.9965 CenterY=107.79 CenterZ=0 NormalX=0 NormalY=0 NormalZ=1 AngleXU=0 Radius=1
    g296: BSplineCurve PolesCount=3 KnotsCount=2 Degree=2 IsPeriodic=0
    g297: GeomPoint X=35.5028 Y=105.865 Z=0
    g298: GeomPoint X=27.9965 Y=107.79 Z=0
    g299: LineSegment StartX=2.07281 StartY=124.221 StartZ=0 EndX=42.0728 EndY=124.221 EndZ=0
    g300: LineSegment StartX=46.0728 StartY=120.221 StartZ=0 EndX=46.0728 EndY=109.865 EndZ=0
    g301: LineSegment StartX=42.0728 StartY=105.865 StartZ=0 EndX=35.5028 EndY=105.865 EndZ=0
    g302: LineSegment StartX=27.9965 StartY=107.79 StartZ=0 EndX=1.57905 EndY=122.295 EndZ=0
    g303: Circle CenterX=42.5666 CenterY=-67.3492 CenterZ=0 NormalX=0 NormalY=0 NormalZ=1 AngleXU=0 Radius=1
    g304: Circle CenterX=46.0728 CenterY=-65.424 CenterZ=0 NormalX=0 NormalY=0 NormalZ=1 AngleXU=0 Radius=1
    g305: Circle CenterX=46.0728 CenterY=-69.424 CenterZ=0 NormalX=0 NormalY=0 NormalZ=1 AngleXU=0 Radius=1
    g306: BSplineCurve PolesCount=3 KnotsCount=2 Degree=2 IsPeriodic=0
    g307: GeomPoint X=42.5666 Y=-67.3492 Z=0
    g308: GeomPoint X=46.0728 Y=-69.424 Z=0
    g309: Circle CenterX=46.0728 CenterY=-87.7794 CenterZ=0 NormalX=0 NormalY=0 NormalZ=1 AngleXU=0 Radius=1
    g310: Circle CenterX=46.0728 CenterY=-91.7794 CenterZ=0 NormalX=0 NormalY=0 NormalZ=1 AngleXU=0 Radius=1
    g311: Circle CenterX=42.0728 CenterY=-91.7794 CenterZ=0 NormalX=0 NormalY=0 NormalZ=1 AngleXU=0 Radius=1
    g312: BSplineCurve PolesCount=3 KnotsCount=2 Degree=2 IsPeriodic=0
    g313: GeomPoint X=46.0728 Y=-87.7794 Z=0
    g314: GeomPoint X=42.0728 Y=-91.7794 Z=0
    g315: Circle CenterX=2.07281 CenterY=-91.7794 CenterZ=0 NormalX=0 NormalY=0 NormalZ=1 AngleXU=0 Radius=1
    g316: Circle CenterX=-1.92719 CenterY=-91.7794 CenterZ=0 NormalX=0 NormalY=0 NormalZ=1 AngleXU=0 Radius=1
    g317: Circle CenterX=1.57905 CenterY=-89.8542 CenterZ=0 NormalX=0 NormalY=0 NormalZ=1 AngleXU=0 Radius=1
    g318: BSplineCurve PolesCount=3 KnotsCount=2 Degree=2 IsPeriodic=0
    g319: GeomPoint X=2.07281 Y=-91.7794 Z=0
    g320: GeomPoint X=1.57905 Y=-89.8542 Z=0
    g321: LineSegment StartX=2.07281 StartY=-91.7794 StartZ=0 EndX=42.0728 EndY=-91.7794 EndZ=0
    g322: LineSegment StartX=46.0728 StartY=-87.7794 StartZ=0 EndX=46.0728 EndY=-69.424 EndZ=0
    g323: LineSegment StartX=42.5666 StartY=-67.3492 StartZ=0 EndX=1.57905 EndY=-89.8542 EndZ=0
    g324: Circle CenterX=322.073 CenterY=76.4095 CenterZ=0 NormalX=0 NormalY=0 NormalZ=1 AngleXU=0 Radius=4
    g325: BSplineCurve PolesCount=3 KnotsCount=2 Degree=2 IsPeriodic=0
    g326: GeomPoint X=318.073 Y=72.4095 Z=0
    g327: GeomPoint X=322.073 Y=76.4095 Z=0
    g328: Circle CenterX=375.073 CenterY=72.4095 CenterZ=0 NormalX=0 NormalY=0 NormalZ=1 AngleXU=0 Radius=1
    g329: Circle CenterX=375.073 CenterY=76.4095 CenterZ=0 NormalX=0 NormalY=0 NormalZ=1 AngleXU=0 Radius=1
    g330: Circle CenterX=371.073 CenterY=76.4095 CenterZ=0 NormalX=0 NormalY=0 NormalZ=1 AngleXU=0 Radius=1
    g331: BSplineCurve PolesCount=3 KnotsCount=2 Degree=2 IsPeriodic=0
    g332: GeomPoint X=375.073 Y=72.4095 Z=0
    g333: GeomPoint X=371.073 Y=76.4095 Z=0
    g334: LineSegment StartX=322.073 StartY=76.4095 StartZ=0 EndX=371.073 EndY=76.4095 EndZ=0
    g335: LineSegment StartX=318.073 StartY=72.4095 StartZ=0 EndX=318.073 EndY=-47.4805 EndZ=0
    g336: LineSegment StartX=375.073 StartY=72.4095 StartZ=0 EndX=375.073 EndY=-78.7896 EndZ=0
    g337: ArcOfCircle CenterX=-26.9272 CenterY=22.1087 CenterZ=0 NormalX=0 NormalY=0 NormalZ=1 AngleXU=0 Radius=4 StartAngle=5e-16 EndAngle=3.14159
    g338: LineSegment StartX=-22.9272 StartY=22.1087 StartZ=0 EndX=-18.9272 EndY=-83.7794 EndZ=0
    g339: LineSegment StartX=-34.9272 StartY=-83.7794 StartZ=0 EndX=-30.9272 EndY=22.1087 EndZ=0
    g340: ArcOfCircle CenterX=391.073 CenterY=22.1087 CenterZ=0 NormalX=0 NormalY=0 NormalZ=1 AngleXU=0 Radius=4 StartAngle=0 EndAngle=3.14159
    g341: LineSegment StartX=387.073 StartY=22.1087 StartZ=0 EndX=383.073 EndY=-83.7794 EndZ=0
    g342: LineSegment StartX=395.073 StartY=22.1087 StartZ=0 EndX=399.073 EndY=-83.7794 EndZ=0
    g343: Circle CenterX=-10.9272 CenterY=-78.7794 CenterZ=0 NormalX=0 NormalY=0 NormalZ=1 AngleXU=0 Radius=1
    g344: Circle CenterX=-10.9272 CenterY=-82.7794 CenterZ=0 NormalX=0 NormalY=0 NormalZ=1 AngleXU=0 Radius=1
    g345: Circle CenterX=-7.42095 CenterY=-80.8542 CenterZ=0 NormalX=0 NormalY=0 NormalZ=1 AngleXU=0 Radius=1
    g346: BSplineCurve PolesCount=3 KnotsCount=2 Degree=2 IsPeriodic=0
    g347: GeomPoint X=-10.9272 Y=-78.7794 Z=0
    g348: GeomPoint X=-7.42095 Y=-80.8542 Z=0
    g349: Circle CenterX=42.5666 CenterY=-53.4075 CenterZ=0 NormalX=0 NormalY=0 NormalZ=1 AngleXU=0 Radius=1
    g350: Circle CenterX=46.0728 CenterY=-51.4823 CenterZ=0 NormalX=0 NormalY=0 NormalZ=1 AngleXU=0 Radius=1
    g351: Circle CenterX=46.0728 CenterY=-47.4823 CenterZ=0 NormalX=0 NormalY=0 NormalZ=1 AngleXU=0 Radius=1
    g352: BSplineCurve PolesCount=3 KnotsCount=2 Degree=2 IsPeriodic=0
    g353: GeomPoint X=42.5666 Y=-53.4075 Z=0
    g354: GeomPoint X=46.0728 Y=-47.4823 Z=0
    g355: Circle CenterX=46.0728 CenterY=72.4095 CenterZ=0 NormalX=0 NormalY=0 NormalZ=1 AngleXU=0 Radius=1
    g356: Circle CenterX=46.0728 CenterY=76.4095 CenterZ=0 NormalX=0 NormalY=0 NormalZ=1 AngleXU=0 Radius=1
    g357: Circle CenterX=42.0728 CenterY=76.4095 CenterZ=0 NormalX=0 NormalY=0 NormalZ=1 AngleXU=0 Radius=1
    g358: BSplineCurve PolesCount=3 KnotsCount=2 Degree=2 IsPeriodic=0
    g359: GeomPoint X=46.0728 Y=72.4095 Z=0
    g360: GeomPoint X=42.0728 Y=76.4095 Z=0
    g361: Circle CenterX=-6.92718 CenterY=76.4095 CenterZ=0 NormalX=0 NormalY=0 NormalZ=1 AngleXU=0 Radius=1
    g362: Circle CenterX=-10.9272 CenterY=76.4095 CenterZ=0 NormalX=0 NormalY=0 NormalZ=1 AngleXU=0 Radius=1
    g363: Circle CenterX=-10.9272 CenterY=72.4095 CenterZ=0 NormalX=0 NormalY=0 NormalZ=1 AngleXU=0 Radius=1
    g364: BSplineCurve PolesCount=3 KnotsCount=2 Degree=2 IsPeriodic=0
    g365: GeomPoint X=-6.92718 Y=76.4095 Z=0
    g366: GeomPoint X=-10.9272 Y=72.4095 Z=0
    g367: LineSegment StartX=-10.9272 StartY=72.4095 StartZ=0 EndX=-10.9272 EndY=-78.7794 EndZ=0
    g368: LineSegment StartX=-7.42095 StartY=-80.8542 StartZ=0 EndX=42.5666 EndY=-53.4075 EndZ=0
    g369: LineSegment StartX=46.0728 StartY=-47.4823 StartZ=0 EndX=46.0728 EndY=72.4095 EndZ=0
    g370: LineSegment StartX=42.0728 StartY=76.4095 StartZ=0 EndX=-6.92719 EndY=76.4095 EndZ=0
    g371: LineSegment StartX=232.072 StartY=136.221 StartZ=0 EndX=232.072 EndY=-117.815 EndZ=0
    g372: LineSegment StartX=132.072 StartY=136.221 StartZ=0 EndX=132.072 EndY=-121.309 EndZ=0
    g373: LineSegment StartX=245.072 StartY=136.221 StartZ=0 EndX=245.072 EndY=-116.499 EndZ=0
    g374: LineSegment StartX=119.072 StartY=136.221 StartZ=0 EndX=119.072 EndY=-116.228 EndZ=0
    g375: LineSegment StartX=-42.9272 StartY=136.221 StartZ=0 EndX=407.073 EndY=136.221 EndZ=0
    g376: LineSegment StartX=232.072 StartY=136.221 StartZ=0 EndX=220.072 EndY=136.221 EndZ=0
    g377: LineSegment StartX=232.072 StartY=136.221 StartZ=0 EndX=232.072 EndY=124.221 EndZ=0
    g378: LineSegment StartX=220.072 StartY=136.221 StartZ=0 EndX=220.072 EndY=124.221 EndZ=0
    g379: LineSegment StartX=220.072 StartY=136.221 StartZ=0 EndX=226.072 EndY=136.221 EndZ=0
    g380: LineSegment StartX=220.072 StartY=136.221 StartZ=0 EndX=220.072 EndY=130.221 EndZ=0
    g381: LineSegment StartX=220.072 StartY=124.221 StartZ=0 EndX=226.072 EndY=124.221 EndZ=0
    g382: LineSegment StartX=232.072 StartY=124.221 StartZ=0 EndX=232.072 EndY=127.021 EndZ=0
    g383: LineSegment StartX=232.072 StartY=136.221 StartZ=0 EndX=232.072 EndY=133.421 EndZ=0
  constraints (644):
    c: Vertical(g0)
    c: Vertical(g1)
    c: Block(g1)
    c: Block(g0)
    c: Weight(g4) = 1
    c: Equal(g4,g5)
    c: Equal(g4,g6)
    c: InternalAlignment(g4,g7)
    c: InternalAlignment(g5,g7)
    c: InternalAlignment(g6,g7)
    c: InternalAlignment(g8,g7)
    c: InternalAlignment(g9,g7)
    c: Weight(g10) = 1
    c: Equal(g10,g11)
    c: Equal(g10,g12)
    c: InternalAlignment(g10,g13)
    c: InternalAlignment(g11,g13)
    c: InternalAlignment(g12,g13)
    c: InternalAlignment(g14,g13)
    c: InternalAlignment(g15,g13)
    c: Block(g13)
    c: Block(g7)
    c: Weight(g16) = 1
    c: Equal(g16,g17)
    c: Equal(g16,g18)
    c: InternalAlignment(g16,g19)
    c: InternalAlignment(g17,g19)
    c: InternalAlignment(g18,g19)
    c: InternalAlignment(g20,g19)
    c: InternalAlignment(g21,g19)
    c: Weight(g22) = 1
    c: Equal(g22,g23)
    c: Equal(g22,g24)
    c: InternalAlignment(g22,g25)
    c: InternalAlignment(g23,g25)
    c: InternalAlignment(g24,g25)
    c: InternalAlignment(g26,g25)
    c: InternalAlignment(g27,g25)
    c: Block(g25)
    c: Block(g19)
    c: Weight(g28) = 1
    c: Equal(g28,g29)
    c: Equal(g28,g30)
    c: InternalAlignment(g28,g31)
    c: InternalAlignment(g29,g31)
    c: InternalAlignment(g30,g31)
    c: InternalAlignment(g32,g31)
    c: InternalAlignment(g33,g31)
    c: Weight(g34) = 1
    c: Equal(g34,g35)
    c: Equal(g34,g36)
    c: InternalAlignment(g34,g37)
    c: InternalAlignment(g35,g37)
    c: InternalAlignment(g36,g37)
    c: InternalAlignment(g38,g37)
    c: InternalAlignment(g39,g37)
    c: Block(g31)
    c: Block(g37)
    c: Coincident(g40,g1)
    c: Coincident(g40,g0)
    c: Horizontal(g40)
    c: Distance(g40) = 450
    c: Weight(g41) = 1
    c: Equal(g41,g42)
    c: Equal(g41,g43)
    c: InternalAlignment(g41,g44)
    c: InternalAlignment(g42,g44)
    c: InternalAlignment(g43,g44)
    c: InternalAlignment(g45,g44)
    c: InternalAlignment(g46,g44)
    c: Block(g44)
    c: Weight(g47) = 1
    c: Equal(g47,g48)
    c: Equal(g47,g49)
    c: InternalAlignment(g47,g50)
    c: InternalAlignment(g48,g50)
    c: InternalAlignment(g49,g50)
    c: InternalAlignment(g51,g50)
    c: InternalAlignment(g52,g50)
    c: Block(g50)
    c: Weight(g53) = 1
    c: Equal(g53,g54)
    c: Equal(g53,g55)
    c: InternalAlignment(g53,g56)
    c: InternalAlignment(g54,g56)
    c: InternalAlignment(g55,g56)
    c: InternalAlignment(g57,g56)
    c: InternalAlignment(g58,g56)
    c: Block(g56)
    c: Weight(g59) = 1
    c: Equal(g59,g60)
    c: Equal(g59,g61)
    c: InternalAlignment(g59,g62)
    c: InternalAlignment(g60,g62)
    c: InternalAlignment(g61,g62)
    c: InternalAlignment(g63,g62)
    c: InternalAlignment(g64,g62)
    c: Block(g62)
    c: Weight(g65) = 1
    c: Equal(g65,g66)
    c: Equal(g65,g67)
    c: InternalAlignment(g65,g68)
    c: InternalAlignment(g66,g68)
    c: InternalAlignment(g67,g68)
    c: InternalAlignment(g69,g68)
    c: InternalAlignment(g70,g68)
    c: Weight(g71) = 1
    c: Equal(g71,g72)
    c: Equal(g71,g73)
    c: InternalAlignment(g71,g74)
    c: InternalAlignment(g72,g74)
    c: InternalAlignment(g73,g74)
    c: InternalAlignment(g75,g74)
    c: InternalAlignment(g76,g74)
    c: Block(g68)
    c: Block(g74)
    c: Coincident(g77,g68)
    c: Coincident(g77,g74)
    c: Vertical(g77)
    c: Coincident(g78,g68)
    c: Coincident(g78,g50)
    c: Coincident(g79,g50)
    c: Coincident(g79,g74)
    c: Weight(g80) = 1
    c: Equal(g80,g81)
    c: Equal(g80,g82)
    c: InternalAlignment(g80,g83)
    c: InternalAlignment(g81,g83)
    c: InternalAlignment(g82,g83)
    c: InternalAlignment(g84,g83)
    c: InternalAlignment(g85,g83)
    c: Weight(g86) = 1
    c: Equal(g86,g87)
    c: Equal(g86,g88)
    c: InternalAlignment(g86,g89)
    c: InternalAlignment(g87,g89)
    c: InternalAlignment(g88,g89)
    c: InternalAlignment(g90,g89)
    c: InternalAlignment(g91,g89)
    c: Block(g83)
    c: Block(g89)
    c: Coincident(g92,g83)
    c: Coincident(g92,g89)
    c: Vertical(g92)
    c: Coincident(g93,g83)
    c: Coincident(g93,g44)
    c: Coincident(g94,g44)
    c: Coincident(g94,g89)
    c: Weight(g95) = 1
    c: Equal(g95,g96)
    c: Equal(g95,g97)
    c: InternalAlignment(g95,g98)
    c: InternalAlignment(g96,g98)
    c: InternalAlignment(g97,g98)
    c: InternalAlignment(g99,g98)
    c: InternalAlignment(g100,g98)
    c: Weight(g101) = 1
    c: Equal(g101,g102)
    c: Equal(g101,g103)
    c: InternalAlignment(g101,g104)
    c: InternalAlignment(g102,g104)
    c: InternalAlignment(g103,g104)
    c: InternalAlignment(g105,g104)
    c: InternalAlignment(g106,g104)
    c: Block(g98)
    c: Block(g104)
    c: Coincident(g107,g98)
    c: Coincident(g107,g104)
    c: Vertical(g107)
    c: Coincident(g108,g104)
    c: Coincident(g108,g62)
    c: Coincident(g109,g62)
    c: Coincident(g109,g98)
    c: Weight(g110) = 1
    c: Equal(g110,g111)
    c: Equal(g110,g112)
    c: InternalAlignment(g110,g113)
    c: InternalAlignment(g111,g113)
    c: InternalAlignment(g112,g113)
    c: InternalAlignment(g114,g113)
    c: InternalAlignment(g115,g113)
    c: Weight(g116) = 1
    c: Equal(g116,g117)
    c: Equal(g116,g118)
    c: InternalAlignment(g116,g119)
    c: InternalAlignment(g117,g119)
    c: InternalAlignment(g118,g119)
    c: InternalAlignment(g120,g119)
    c: InternalAlignment(g121,g119)
    c: Block(g113)
    c: Block(g119)
    c: Coincident(g122,g113)
    c: Coincident(g122,g119)
    c: Vertical(g122)
    c: Coincident(g123,g119)
    c: Coincident(g123,g56)
    c: Coincident(g124,g56)
    c: Coincident(g124,g113)
    c: Weight(g125) = 1
    c: Equal(g125,g126)
    c: Equal(g125,g127)
    c: InternalAlignment(g125,g128)
    c: InternalAlignment(g126,g128)
    c: InternalAlignment(g127,g128)
    c: InternalAlignment(g129,g128)
    c: InternalAlignment(g130,g128)
    c: Weight(g131) = 1
    c: Equal(g131,g132)
    c: Equal(g131,g133)
    c: InternalAlignment(g131,g134)
    c: InternalAlignment(g132,g134)
    c: InternalAlignment(g133,g134)
    c: InternalAlignment(g135,g134)
    c: InternalAlignment(g136,g134)
    c: Weight(g137) = 1
    c: Equal(g137,g138)
    c: Equal(g137,g139)
    c: InternalAlignment(g137,g140)
    c: InternalAlignment(g138,g140)
    c: InternalAlignment(g139,g140)
    c: InternalAlignment(g141,g140)
    c: InternalAlignment(g142,g140)
    c: Weight(g143) = 1
    c: Equal(g143,g144)
    c: Equal(g143,g145)
    c: InternalAlignment(g143,g146)
    c: InternalAlignment(g144,g146)
    c: InternalAlignment(g145,g146)
    c: InternalAlignment(g147,g146)
    c: InternalAlignment(g148,g146)
    c: Block(g146)
    c: Block(g140)
    c: Block(g134)
    c: Block(g128)
    c: Coincident(g149,g25)
    c: Coincident(g149,g146)
    c: Coincident(g150,g146)
    c: Coincident(g150,g140)
    c: Horizontal(g150)
    c: Coincident(g151,g140)
    c: Coincident(g151,g25)
    c: Vertical(g151)
    c: Coincident(g152,g19)
    c: Coincident(g152,g134)
    c: Vertical(g152)
    c: Coincident(g153,g134)
    c: Coincident(g153,g128)
    c: Horizontal(g153)
    c: Coincident(g154,g128)
    c: Coincident(g154,g19)
    c: Weight(g155) = 1
    c: Equal(g155,g156)
    c: Equal(g155,g157)
    c: InternalAlignment(g155,g158)
    c: InternalAlignment(g156,g158)
    c: InternalAlignment(g157,g158)
    c: InternalAlignment(g159,g158)
    c: InternalAlignment(g160,g158)
    c: Weight(g161) = 1
    c: Equal(g161,g162)
    c: Equal(g161,g163)
    c: InternalAlignment(g161,g164)
    c: InternalAlignment(g162,g164)
    c: InternalAlignment(g163,g164)
    c: InternalAlignment(g165,g164)
    c: InternalAlignment(g166,g164)
    c: Weight(g167) = 1
    c: Equal(g167,g168)
    c: Equal(g167,g169)
    c: InternalAlignment(g167,g170)
    c: InternalAlignment(g168,g170)
    c: InternalAlignment(g169,g170)
    c: InternalAlignment(g171,g170)
    c: InternalAlignment(g172,g170)
    c: Weight(g173) = 1
    c: Equal(g173,g174)
    c: Equal(g173,g175)
    c: InternalAlignment(g173,g176)
    c: InternalAlignment(g174,g176)
    c: InternalAlignment(g175,g176)
    c: InternalAlignment(g177,g176)
    c: InternalAlignment(g178,g176)
    c: Block(g176)
    c: Block(g170)
    c: Block(g164)
    c: Block(g158)
    c: Coincident(g179,g176)
    c: Coincident(g179,g170)
    c: Horizontal(g179)
    c: Coincident(g180,g170)
    c: Coincident(g180,g7)
    c: Vertical(g180)
    c: Coincident(g181,g13)
    c: Coincident(g181,g164)
    c: Vertical(g181)
    c: Coincident(g182,g158)
    c: Coincident(g182,g13)
    c: Coincident(g183,g7)
    c: Weight(g184) = 1
    c: Equal(g184,g185)
    c: Equal(g184,g186)
    c: InternalAlignment(g184,g187)
    c: InternalAlignment(g185,g187)
    c: InternalAlignment(g186,g187)
    c: InternalAlignment(g188,g187)
    c: InternalAlignment(g189,g187)
    c: Weight(g190) = 1
    c: Equal(g190,g191)
    c: Equal(g190,g192)
    c: InternalAlignment(g190,g193)
    c: InternalAlignment(g191,g193)
    c: InternalAlignment(g192,g193)
    c: InternalAlignment(g194,g193)
    c: InternalAlignment(g195,g193)
    c: Block(g193)
    c: Block(g187)
    c: Coincident(g196,g193)
    c: Coincident(g196,g31)
    c: Coincident(g197,g31)
    c: Coincident(g197,g187)
    c: Coincident(g198,g187)
    c: Coincident(g198,g193)
    c: Vertical(g198)
    c: Weight(g199) = 1
    c: Equal(g199,g200)
    c: Equal(g199,g201)
    c: InternalAlignment(g199,g202)
    c: InternalAlignment(g200,g202)
    c: InternalAlignment(g201,g202)
    c: InternalAlignment(g203,g202)
    c: InternalAlignment(g204,g202)
    c: Weight(g205) = 1
    c: Equal(g205,g206)
    c: Equal(g205,g207)
    c: InternalAlignment(g205,g208)
    c: InternalAlignment(g206,g208)
    c: InternalAlignment(g207,g208)
    c: InternalAlignment(g209,g208)
    c: InternalAlignment(g210,g208)
    c: Block(g208)
    c: Block(g202)
    c: Coincident(g211,g202)
    c: Coincident(g211,g37)
    c: Coincident(g212,g37)
    c: Coincident(g212,g208)
    c: Coincident(g213,g208)
    c: Coincident(g213,g202)
    c: Vertical(g213)
    c: Horizontal(g214)
    c: Block(g214)
    c: Vertical(g215)
    c: Block(g215)
    c: Block(g216)
    c: Weight(g217) = 1
    c: Equal(g217,g218)
    c: Equal(g217,g219)
    c: InternalAlignment(g217,g220)
    c: InternalAlignment(g218,g220)
    c: InternalAlignment(g219,g220)
    c: InternalAlignment(g221,g220)
    c: InternalAlignment(g222,g220)
    c: Weight(g223) = 1
    c: Equal(g223,g224)
    c: Equal(g223,g225)
    c: InternalAlignment(g223,g226)
    c: InternalAlignment(g224,g226)
    c: InternalAlignment(g225,g226)
    c: InternalAlignment(g227,g226)
    c: InternalAlignment(g228,g226)
    c: Weight(g229) = 1
    c: Equal(g229,g230)
    c: Equal(g229,g231)
    c: InternalAlignment(g229,g232)
    c: InternalAlignment(g230,g232)
    c: InternalAlignment(g231,g232)
    c: InternalAlignment(g233,g232)
    c: InternalAlignment(g234,g232)
    c: Weight(g235) = 1
    c: Equal(g235,g236)
    c: Equal(g235,g237)
    c: InternalAlignment(g235,g238)
    c: InternalAlignment(g236,g238)
    c: InternalAlignment(g237,g238)
    c: InternalAlignment(g239,g238)
    c: InternalAlignment(g240,g238)
    c: Block(g220)
    c: Block(g226)
    c: Block(g232)
    c: Block(g238)
    c: Coincident(g241,g226)
    c: Coincident(g241,g220)
    c: Horizontal(g241)
    c: Block(g183)
    c: Weight(g242) = 1
    c: Equal(g242,g243)
    c: Equal(g242,g244)
    c: InternalAlignment(g242,g245)
    c: InternalAlignment(g243,g245)
    c: InternalAlignment(g244,g245)
    c: InternalAlignment(g246,g245)
    c: InternalAlignment(g247,g245)
    c: Weight(g248) = 1
    c: Equal(g248,g249)
    c: Equal(g248,g250)
    c: InternalAlignment(g248,g251)
    c: InternalAlignment(g249,g251)
    c: InternalAlignment(g250,g251)
    c: InternalAlignment(g252,g251)
    c: InternalAlignment(g253,g251)
    c: Block(g245)
    c: Block(g251)
    c: Coincident(g254,g245)
    c: Coincident(g254,g251)
    c: Weight(g255) = 1
    c: Equal(g255,g256)
    c: Equal(g255,g257)
    c: InternalAlignment(g255,g258)
    c: InternalAlignment(g256,g258)
    c: InternalAlignment(g257,g258)
    c: InternalAlignment(g259,g258)
    c: InternalAlignment(g260,g258)
    c: Weight(g261) = 1
    c: Equal(g261,g262)
    c: Equal(g261,g263)
    c: InternalAlignment(g261,g264)
    c: InternalAlignment(g262,g264)
    c: InternalAlignment(g263,g264)
    c: InternalAlignment(g265,g264)
    c: InternalAlignment(g266,g264)
    c: Weight(g267) = 1
    c: Equal(g267,g268)
    c: Equal(g267,g269)
    c: InternalAlignment(g267,g270)
    c: InternalAlignment(g268,g270)
    c: InternalAlignment(g269,g270)
    c: InternalAlignment(g271,g270)
    c: InternalAlignment(g272,g270)
    c: Block(g270)
    c: Block(g264)
    c: Block(g258)
    c: Coincident(g273,g264)
    c: Coincident(g273,g258)
    c: Coincident(g274,g258)
    c: Coincident(g274,g270)
    c: Vertical(g274)
    c: Coincident(g275,g270)
    c: Coincident(g275,g264)
    c: Horizontal(g275)
    c: Weight(g276) = 1
    c: Equal(g276,g277)
    c: InternalAlignment(g276,g278)
    c: InternalAlignment(g277,g278)
    c: InternalAlignment(g279,g278)
    c: InternalAlignment(g280,g278)
    c: Weight(g281) = 1
    c: InternalAlignment(g282,g284)
    c: InternalAlignment(g283,g284)
    c: InternalAlignment(g285,g284)
    c: InternalAlignment(g286,g284)
    c: Weight(g287) = 1
    c: Equal(g287,g288)
    c: Equal(g287,g289)
    c: InternalAlignment(g287,g290)
    c: InternalAlignment(g288,g290)
    c: InternalAlignment(g289,g290)
    c: InternalAlignment(g291,g290)
    c: InternalAlignment(g292,g290)
    c: Equal(g293,g294)
    c: Equal(g293,g295)
    c: InternalAlignment(g293,g296)
    c: InternalAlignment(g294,g296)
    c: InternalAlignment(g295,g296)
    c: InternalAlignment(g297,g296)
    c: InternalAlignment(g298,g296)
    c: Block(g284)
    c: Block(g290)
    c: Block(g296)
    c: Block(g278)
    c: Coincident(g299,g278)
    c: Coincident(g299,g284)
    c: Horizontal(g299)
    c: Coincident(g300,g284)
    c: Coincident(g300,g290)
    c: Vertical(g300)
    c: Coincident(g301,g290)
    c: Coincident(g301,g296)
    c: Horizontal(g301)
    c: Coincident(g302,g296)
    c: Coincident(g302,g278)
    c: Weight(g303) = 1
    c: Equal(g303,g304)
    c: Equal(g303,g305)
    c: InternalAlignment(g303,g306)
    c: InternalAlignment(g304,g306)
    c: InternalAlignment(g305,g306)
    c: InternalAlignment(g307,g306)
    c: InternalAlignment(g308,g306)
    c: Weight(g309) = 1
    c: Equal(g309,g310)
    c: Equal(g309,g311)
    c: InternalAlignment(g309,g312)
    c: InternalAlignment(g310,g312)
    c: InternalAlignment(g311,g312)
    c: InternalAlignment(g313,g312)
    c: InternalAlignment(g314,g312)
    c: Weight(g315) = 1
    c: Equal(g315,g316)
    c: Equal(g315,g317)
    c: InternalAlignment(g315,g318)
    c: InternalAlignment(g316,g318)
    c: InternalAlignment(g317,g318)
    c: InternalAlignment(g319,g318)
    c: InternalAlignment(g320,g318)
    c: Block(g318)
    c: Block(g312)
    c: Block(g306)
    c: Coincident(g321,g318)
    c: Coincident(g321,g312)
    c: Horizontal(g321)
    c: Coincident(g322,g312)
    c: Coincident(g322,g306)
    c: Vertical(g322)
    c: Coincident(g323,g306)
    c: Coincident(g323,g318)
    c: InternalAlignment(g324,g325)
    c: InternalAlignment(g326,g325)
    c: InternalAlignment(g327,g325)
    c: Block(g325)
    c: Equal(g328,g329)
    c: Equal(g328,g330)
    c: InternalAlignment(g328,g331)
    c: InternalAlignment(g329,g331)
    c: InternalAlignment(g330,g331)
    c: InternalAlignment(g332,g331)
    c: InternalAlignment(g333,g331)
    c: Block(g331)
    c: Coincident(g334,g325)
    c: Horizontal(g334)
    c: Block(g334)
    c: Coincident(g335,g325)
    c: Coincident(g335,g251)
    c: Vertical(g335)
    c: Coincident(g336,g331)
    c: Coincident(g336,g245)
    c: Vertical(g336)
    c: Block(g337)
    c: Block(g2)
    c: Distance(g335) = 119.89
    c: Coincident(g338,g337)
    c: Coincident(g338,g2)
    c: Coincident(g339,g2)
    c: Coincident(g339,g337)
    c: Block(g3)
    c: Block(g340)
    c: Coincident(g341,g340)
    c: Coincident(g341,g3)
    c: Coincident(g342,g340)
    c: Coincident(g342,g3)
    c: Block(g342)
    c: Block(g341)
    c: Weight(g343) = 1
    c: Equal(g343,g344)
    c: Equal(g343,g345)
    c: InternalAlignment(g343,g346)
    c: InternalAlignment(g344,g346)
    c: InternalAlignment(g345,g346)
    c: InternalAlignment(g347,g346)
    c: InternalAlignment(g348,g346)
    c: Weight(g349) = 1
    c: Equal(g349,g350)
    c: Equal(g349,g351)
    c: InternalAlignment(g349,g352)
    c: InternalAlignment(g350,g352)
    c: InternalAlignment(g351,g352)
    c: InternalAlignment(g353,g352)
    c: InternalAlignment(g354,g352)
    c: Weight(g355) = 1
    c: Equal(g355,g356)
    c: Equal(g355,g357)
    c: InternalAlignment(g355,g358)
    c: InternalAlignment(g356,g358)
    c: InternalAlignment(g357,g358)
    c: InternalAlignment(g359,g358)
    c: InternalAlignment(g360,g358)
    c: Weight(g361) = 1
    c: Equal(g361,g362)
    c: Equal(g361,g363)
    c: InternalAlignment(g361,g364)
    c: InternalAlignment(g362,g364)
    c: InternalAlignment(g363,g364)
    c: InternalAlignment(g365,g364)
    c: InternalAlignment(g366,g364)
    c: Block(g364)
    c: Block(g358)
    c: Block(g352)
    c: Block(g346)
    c: Coincident(g367,g364)
    c: Coincident(g367,g346)
    c: Vertical(g367)
    c: Coincident(g368,g346)
    c: Coincident(g368,g352)
    c: Coincident(g369,g352)
    c: Coincident(g369,g358)
    c: Vertical(g369)
    c: Coincident(g370,g358)
    c: Coincident(g370,g364)
    c: Horizontal(g370)
    c: Vertical(g371)
    c: Vertical(g372)
    c: Vertical(g373)
    c: Vertical(g374)
    c: Coincident(g375,g0)
    c: Coincident(g375,g1)
    c: Horizontal(g375)
    c: Block(g375)
    c: Distance(g375) = 450
    c: Block(g373)
    c: Block(g371)
    c: Block(g372)
    c: Block(g374)
    c: Distance(g0) = 240
    c: Horizontal(g376)
    c: Distance(g376) = 12
    c: Coincident(g376,g371)
    c: Vertical(g377)
    c: Distance(g377) = 12
    c: Coincident(g377,g371)
    c: Coincident(g378,g376)
    c: Vertical(g378)
    c: Horizontal(g379)
    c: Vertical(g380)
    c: Distance(g380) = 6
    c: Coincident(g380,g376)
    c: Coincident(g379,g376)
    c: Block(g378)
    c: Coincident(g381,g378)
    c: Horizontal(g381)
    c: Distance(g381) = 6
    c: Vertical(g382)
    c: Distance(g382) = 2.8
    c: Vertical(g383)
    c: Distance(g383) = 2.8
    c: Coincident(g383,g371)
    c: Coincident(g382,g377)
FEATURE [Part::Extrusion] Extrude005
  Base = -> Sketch003
  Dir = (0,0,1)
  DirMode = 2
  FaceMakerClass = Part::FaceMakerBullseye
  LengthFwd = 24
  LengthRev = 0
  Solid = true
  Symmetric = false
